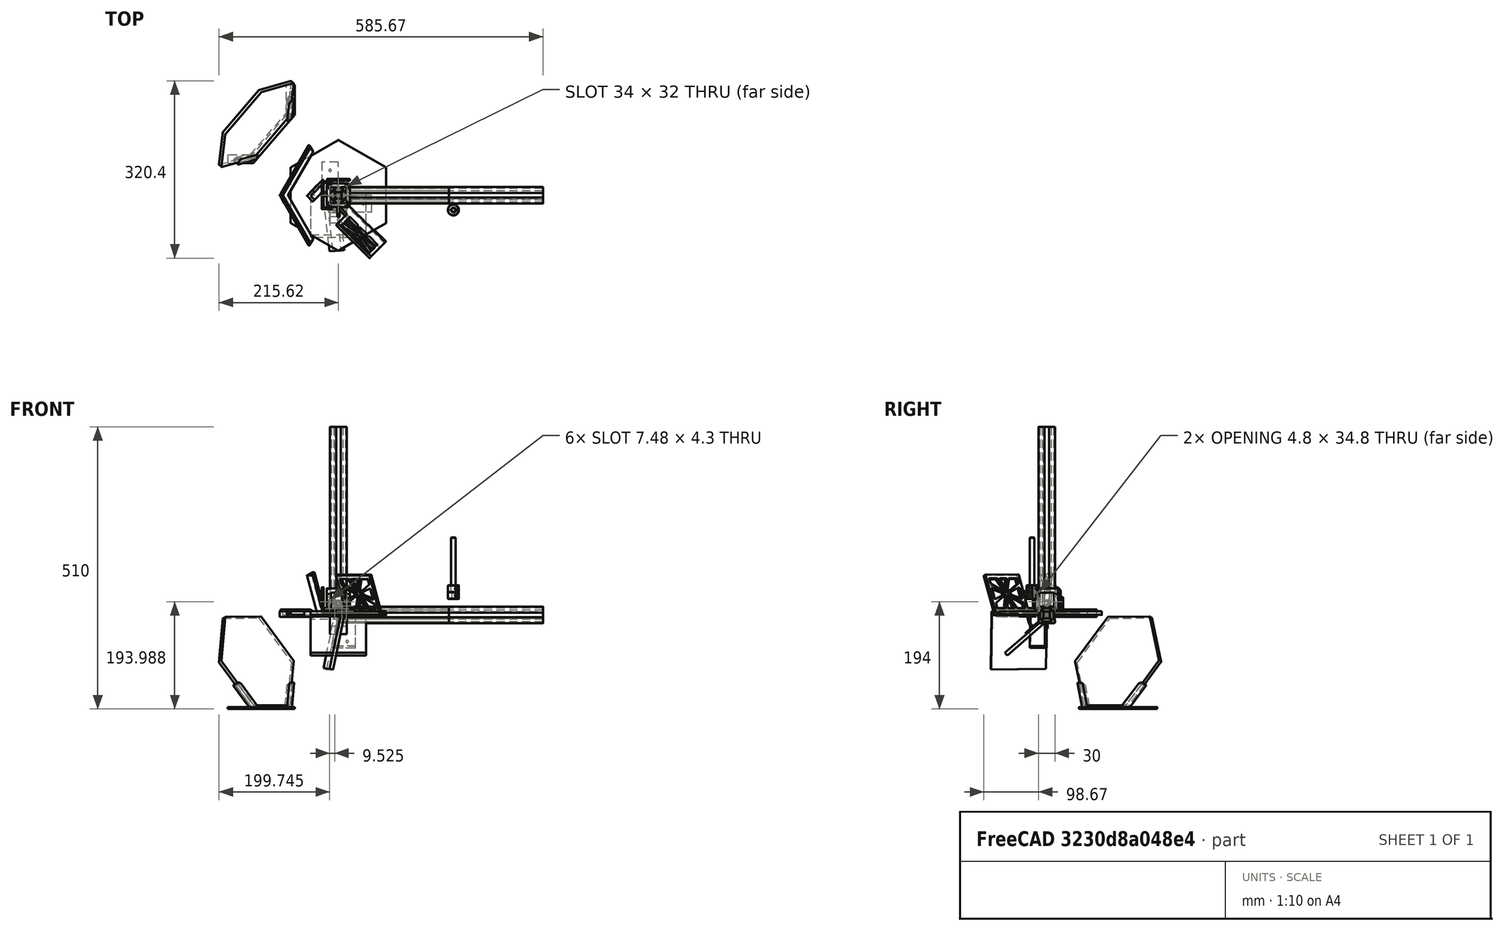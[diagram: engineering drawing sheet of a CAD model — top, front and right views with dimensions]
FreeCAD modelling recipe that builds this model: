
FCSTD DOCUMENT  (FreeCAD 1.1RUnknown)
Label: frame
License: All rights reserved
LicenseURL: https://en.wikipedia.org/wiki/All_rights_reserved
objects: App::Link×33, Sketcher::SketchObject×33, App::Point×32, App::Part×20, PartDesign::Pad×20, Part::Feature×15, PartDesign::Body×12, PartDesign::Fillet×12, PartDesign::Plane×11, PartDesign::Pocket×8, Part::Extrusion×3, Mesh::Feature×3, PartDesign::SubShapeBinder×3, PartDesign::AdditivePipe×2, PartDesign::Boolean×2, PartDesign::SubtractivePipe×2, Spreadsheet::Sheet×1, PartDesign::AdditiveBox×1, Part::Box×1, PartDesign::Mirrored×1, +2 more types
note: 252 computed .brp shape members not serialized (recipe doc carries the construction recipe); baked Part::Feature solids carry a one-line shape summary decoded from their .brp

FEATURE [PartDesign::Body] Body
  AllowCompound = false
  Origin = -> Origin
FEATURE [Spreadsheet::Sheet] Spreadsheet
  cells = A1='Extrusion length:; B1(EL)==200 mm; D1='Extrusion width; E1==30 mm; G1='Mirror thickness; H1==0.25 in; M1='Rail thickness; N1==3 mm; O1==H1 + H6 + N1 * 2; A2='Cube size:; B2==2.2 in; C2==-B2 / 2; D2='Extrusion radius; E2==E1 / 2; G2='Mount thickness; H2==3 mm; M2='Rail width; N2==8 mm; A3='Frame distance:; B3==B1 - B6 + E1; G3='Flange width; H3==8 mm; M3='Rail length; N3==50 mm; A4='Motor distance; B4==170 mm; C4==B4 - 150 mm; D4='Before (152.25mm); G4='Edge width; H4==5 mm; A5='Motor offset; B5==45 mm; G5='Edge height; H5==H1 + H2 + H6 * 2; A6='Inset amount; B6==45 mm; G6='Mirror tolerance; H6==0.5 mm; G7='Mirror width; H7==200 mm; A8='Length 2; B8==B1; A9='Length 3; B9==B3 * 2; G9='Cover height; H9==3 mm; J9='Total height; K9==H5 + H9; A10='Length 4; B10==2 * B3 - E1; G10='Stretch amt; H10==1 mm; G11='Tab thickness; H11==3 mm; A12='Gripper dist; B12==B4 - 9 mm; G12='Tab distance; H12==H7 / 2 + I12; I12==2.5 mm; A14='Robot Radius; B14==B1; G14='Tab width; H14==15 mm; G15='Extra space; H15==10 mm; M15='Square mirror width; N15==100 mm; G16='Tab space; H16==H14 + H15; M16='Mirror 1 angle; N16=41; G18='Pin dist; H18==30 mm; G19='Square dist; H19==H18 - H4 / 2; A20='Phone dims; G20='Pin diameter; H20==3 mm; A21='Height; B21==80 mm; G21='Pin tolerance; H21==0.5 mm; A22='Cameras; B22==70 mm; A23='Phone width; B23==10 mm; G23='Plate Snapper Gap; H23==0.5 mm; A24='Holder width; B24==160 mm
FEATURE [PartDesign::AdditiveBox] Box
  AttacherType = Attacher::AttachEngine3D
  AttachmentOffset = pos=(-27.94,-27.94,-27.94) rot=(0,0,1;0rad)
  AttachmentSupport = -> [XY_Plane002]
  Height = 55.88
  Length = 55.88
  MapMode = 5
  Placement = pos=(-27.94,-27.94,-27.94) rot=(0,0,1;0rad)
  Refine = true
  Suppressed = false
  Width = 55.88
  expr: .AttachmentOffset.Base.x = Spreadsheet.C2
  expr: .AttachmentOffset.Base.y = Spreadsheet.C2
  expr: .AttachmentOffset.Base.z = Spreadsheet.C2
  expr: Height = Spreadsheet.B2
  expr: Length = Spreadsheet.B2
  expr: Width = Spreadsheet.B2
FEATURE [App::Part] Part001  label="Rubik's Cube"
  Group = -> [Box]
  Origin = -> Origin002
FEATURE [Part::Box] Box001  label="Cube"
  AttacherType = Attacher::AttachEngine3D
  Height = 25
  Length = 200
  Placement = pos=(0,-12.5,-12.5) rot=(0,0,1;0rad)
  Width = 25
  expr: Length = Spreadsheet.B1
FEATURE [App::Link] Link001  label="Rubik's Cube001"
  LinkedObject = -> Part001
FEATURE [App::Link] Link004  label="Extrusion004"
  LinkPlacement = pos=(-45,-30,185) rot=(0,0,1;1.5708rad)
  LinkedObject = -> Part
  Placement = pos=(-45,-30,185) rot=(0,0,1;1.5708rad)
  expr: .Placement.Base.x = -Spreadsheet.B5
  expr: .Placement.Base.y = Spreadsheet.E2 - Spreadsheet.B6
  expr: .Placement.Base.z = Spreadsheet.B3
FEATURE [Part::Feature] Part__Feature001  label="bkt08a"
  Placement = pos=(-20.7,26.4,0) rot=(0.707107,0,0.707107;3.14159rad)
  shape: bbox 41.3 x 51 x 35 mm, 84 faces (baked)
FEATURE [App::Link] Link011  label="Motor mount001"
  LinkPlacement = pos=(0,0,170) rot=(0,0,1;1.5708rad)
  LinkedObject = -> Part003
  Placement = pos=(0,0,170) rot=(0,0,1;1.5708rad)
  expr: .Placement.Base.z = Spreadsheet.B4
FEATURE [App::Link] Link012  label="Motor mount002"
  LinkPlacement = pos=(0,170,0) rot=(1,0,0;-1.5708rad)
  LinkedObject = -> Part003
  Placement = pos=(0,170,0) rot=(1,0,0;-1.5708rad)
  expr: .Placement.Base.y = Spreadsheet.B4
FEATURE [App::Link] Link013  label="Motor mount003"
  LinkPlacement = pos=(0,0,-170) rot=(1,0,0;3.14159rad)
  LinkedObject = -> Part003
  Placement = pos=(0,0,-170) rot=(1,0,0;3.14159rad)
  expr: .Placement.Base.z = -Spreadsheet.B4
FEATURE [App::Link] Link014  label="Motor mount004"
  LinkPlacement = pos=(0,-170,0) rot=(1,0,0;1.5708rad)
  LinkedObject = -> Part003
  Placement = pos=(0,-170,0) rot=(1,0,0;1.5708rad)
  expr: .Placement.Base.y = -Spreadsheet.B4
FEATURE [App::Link] Link015  label="Motor mount005"
  LinkPlacement = pos=(170,0,0) rot=(1,-1,1;4.18879rad)
  LinkedObject = -> Part003
  Placement = pos=(170,0,0) rot=(1,-1,1;4.18879rad)
  expr: .Placement.Base.x = Spreadsheet.B4
FEATURE [App::Link] Link016  label="Motor mount006"
  LinkPlacement = pos=(-170,0,0) rot=(1,1,-1;4.18879rad)
  LinkedObject = -> Part003
  Placement = pos=(-170,0,0) rot=(1,1,-1;4.18879rad)
  expr: .Placement.Base.x = -Spreadsheet.B4
FEATURE [Part::Feature] Part__Feature  label="17HS19-2004S1"
  shape: bbox 42.32 x 71.15 x 72 mm, 281 faces (baked)
FEATURE [Sketcher::SketchObject] Sketch001
  ArcFitTolerance = 1e-06
  AttachmentSupport = -> [YZ_Plane]
  ExternalTypes = [0]
  FullyConstrained = true
  MakeInternals = false
  MapMode = 5
  Placement = pos=(0,0,0) rot=(0.57735,0.57735,0.57735;2.0944rad)
  _ExternalGeoVersion = 0
  sketch-geometry (67):
    g0: LineSegment StartX=-3.2886 StartY=5.82 StartZ=0 EndX=3.2886 EndY=5.82 EndZ=0
    g1: LineSegment StartX=-3.2886 StartY=-5.82 StartZ=0 EndX=3.2886 EndY=-5.82 EndZ=0
    g2: LineSegment StartX=5.82 StartY=-3.2886 StartZ=0 EndX=5.82 EndY=3.2886 EndZ=0
    g3: LineSegment StartX=-5.82 StartY=-3.2886 StartZ=0 EndX=-5.82 EndY=3.2886 EndZ=0
    g4: LineSegment [constr] StartX=-15.0006 StartY=-15.0006 StartZ=0 EndX=14.9994 EndY=14.9994 EndZ=0
    g5: ArcOfCircle CenterX=7.59529 CenterY=3.2886 CenterZ=0 NormalX=0 NormalY=0 NormalZ=1 AngleXU=0 Radius=1.77529 StartAngle=2.35619 EndAngle=3.14159
    g6: ArcOfCircle CenterX=3.2886 CenterY=7.59529 CenterZ=0 NormalX=0 NormalY=0 NormalZ=1 AngleXU=0 Radius=1.77529 StartAngle=4.71239 EndAngle=5.49779
    g7: ArcOfCircle CenterX=-3.2886 CenterY=7.59529 CenterZ=0 NormalX=0 NormalY=0 NormalZ=1 AngleXU=0 Radius=1.77529 StartAngle=3.92699 EndAngle=4.71239
    g8: ArcOfCircle CenterX=-7.59529 CenterY=3.2886 CenterZ=0 NormalX=0 NormalY=0 NormalZ=1 AngleXU=0 Radius=1.77529 StartAngle=5e-16 EndAngle=0.785398
    g9: ArcOfCircle CenterX=-7.59529 CenterY=-3.2886 CenterZ=0 NormalX=0 NormalY=0 NormalZ=1 AngleXU=0 Radius=1.77529 StartAngle=5.49779 EndAngle=6.28319
    g10: ArcOfCircle CenterX=-3.2886 CenterY=-7.59529 CenterZ=0 NormalX=0 NormalY=0 NormalZ=1 AngleXU=0 Radius=1.77529 StartAngle=1.5708 EndAngle=2.35619
    g11: ArcOfCircle CenterX=3.2886 CenterY=-7.59529 CenterZ=0 NormalX=0 NormalY=0 NormalZ=1 AngleXU=0 Radius=1.77529 StartAngle=0.785398 EndAngle=1.5708
    g12: ArcOfCircle CenterX=7.59529 CenterY=-3.2886 CenterZ=0 NormalX=0 NormalY=0 NormalZ=1 AngleXU=0 Radius=1.77529 StartAngle=3.14159 EndAngle=3.92699
    g13: LineSegment [constr] StartX=-14.9994 StartY=14.9994 StartZ=0 EndX=15.0006 EndY=-15.0006 EndZ=0
    g14: LineSegment StartX=4.54392 StartY=6.33997 StartZ=0 EndX=7.73503 EndY=9.53108 EndZ=0
    g15: LineSegment StartX=6.33997 StartY=4.54392 StartZ=0 EndX=9.53108 EndY=7.73503 EndZ=0
    g16: LineSegment StartX=6.33997 StartY=-4.54392 StartZ=0 EndX=9.53108 EndY=-7.73503 EndZ=0
    g17: LineSegment StartX=4.54392 StartY=-6.33997 StartZ=0 EndX=7.73503 EndY=-9.53108 EndZ=0
    g18: LineSegment StartX=-4.54392 StartY=-6.33997 StartZ=0 EndX=-7.73503 EndY=-9.53108 EndZ=0
    g19: LineSegment StartX=-6.33997 StartY=-4.54392 StartZ=0 EndX=-9.53108 EndY=-7.73503 EndZ=0
    g20: LineSegment StartX=-4.54392 StartY=6.33997 StartZ=0 EndX=-7.73503 EndY=9.53108 EndZ=0
    g21: LineSegment StartX=-6.33997 StartY=4.54392 StartZ=0 EndX=-9.53108 EndY=7.73503 EndZ=0
    g22: ArcOfCircle CenterX=10.7864 CenterY=6.47971 CenterZ=0 NormalX=0 NormalY=0 NormalZ=1 AngleXU=0 Radius=1.77529 StartAngle=6.24828 EndAngle=8.63938
    g23: LineSegment StartX=12.5606 StartY=6.41776 StartZ=0 EndX=12.5184 EndY=5.20856 EndZ=0
    g24: LineSegment StartX=14.727 StartY=5.13144 StartZ=0 EndX=14.9994 EndY=12.9308 EndZ=0
    g25: ArcOfCircle CenterX=13.6227 CenterY=5.17 CenterZ=0 NormalX=0 NormalY=0 NormalZ=1 AngleXU=0 Radius=1.105 StartAngle=3.10669 EndAngle=6.24828
    g26: ArcOfCircle CenterX=6.47971 CenterY=10.7864 CenterZ=0 NormalX=0 NormalY=0 NormalZ=1 AngleXU=0 Radius=1.77529 StartAngle=5.49779 EndAngle=7.88889
    g27: ArcOfCircle CenterX=5.17 CenterY=13.6227 CenterZ=0 NormalX=0 NormalY=0 NormalZ=1 AngleXU=0 Radius=1.105 StartAngle=1.6057 EndAngle=4.7473
    g28: LineSegment StartX=5.20856 StartY=12.5184 StartZ=0 EndX=6.41776 EndY=12.5606 EndZ=0
    g29: LineSegment StartX=5.13144 StartY=14.727 StartZ=0 EndX=12.9308 EndY=14.9994 EndZ=0
    g30: ArcOfCircle CenterX=13.0006 CenterY=13.0006 CenterZ=0 NormalX=0 NormalY=0 NormalZ=1 AngleXU=0 Radius=2 StartAngle=6.24828 EndAngle=7.88889
    g31: LineSegment [constr] StartX=12.9308 StartY=14.9994 StartZ=0 EndX=14.9994 EndY=14.9994 EndZ=0
    g32: ArcOfCircle CenterX=-6.47971 CenterY=10.7864 CenterZ=0 NormalX=0 NormalY=0 NormalZ=1 AngleXU=0 Radius=1.77529 StartAngle=1.53589 EndAngle=3.92699
    g33: LineSegment StartX=-6.41776 StartY=12.5606 StartZ=0 EndX=-5.20856 EndY=12.5184 EndZ=0
    g34: LineSegment StartX=-5.13144 StartY=14.727 StartZ=0 EndX=-12.9308 EndY=14.9994 EndZ=0
    g35: ArcOfCircle CenterX=-5.17 CenterY=13.6227 CenterZ=0 NormalX=0 NormalY=0 NormalZ=1 AngleXU=0 Radius=1.105 StartAngle=4.67748 EndAngle=7.81907
    g36: ArcOfCircle CenterX=-10.7864 CenterY=6.47971 CenterZ=0 NormalX=0 NormalY=0 NormalZ=1 AngleXU=0 Radius=1.77529 StartAngle=0.785398 EndAngle=3.1765
    g37: ArcOfCircle CenterX=-13.6227 CenterY=5.17 CenterZ=0 NormalX=0 NormalY=0 NormalZ=1 AngleXU=0 Radius=1.105 StartAngle=3.1765 EndAngle=6.31809
    g38: LineSegment StartX=-12.5184 StartY=5.20856 StartZ=0 EndX=-12.5606 EndY=6.41776 EndZ=0
    g39: LineSegment StartX=-14.727 StartY=5.13144 StartZ=0 EndX=-14.9994 EndY=12.9308 EndZ=0
    g40: ArcOfCircle CenterX=-13.0006 CenterY=13.0006 CenterZ=0 NormalX=0 NormalY=0 NormalZ=1 AngleXU=0 Radius=2 StartAngle=1.53589 EndAngle=3.1765
    g41: ArcOfCircle CenterX=-10.7864 CenterY=-6.47971 CenterZ=0 NormalX=0 NormalY=0 NormalZ=1 AngleXU=0 Radius=1.77529 StartAngle=3.10669 EndAngle=5.49779
    g42: LineSegment StartX=-12.5606 StartY=-6.41776 StartZ=0 EndX=-12.5184 EndY=-5.20856 EndZ=0
    g43: LineSegment StartX=-14.727 StartY=-5.13144 StartZ=0 EndX=-14.9994 EndY=-12.9308 EndZ=0
    g44: ArcOfCircle CenterX=-13.6227 CenterY=-5.17 CenterZ=0 NormalX=0 NormalY=0 NormalZ=1 AngleXU=0 Radius=1.105 StartAngle=6.24828 EndAngle=9.38987
    g45: ArcOfCircle CenterX=-6.47971 CenterY=-10.7864 CenterZ=0 NormalX=0 NormalY=0 NormalZ=1 AngleXU=0 Radius=1.77529 StartAngle=2.35619 EndAngle=4.7473
    g46: ArcOfCircle CenterX=-5.17 CenterY=-13.6227 CenterZ=0 NormalX=0 NormalY=0 NormalZ=1 AngleXU=0 Radius=1.105 StartAngle=4.7473 EndAngle=7.88889
    g47: LineSegment StartX=-5.20856 StartY=-12.5184 StartZ=0 EndX=-6.41776 EndY=-12.5606 EndZ=0
    g48: LineSegment StartX=-5.13144 StartY=-14.727 StartZ=0 EndX=-12.9308 EndY=-14.9994 EndZ=0
    g49: ArcOfCircle CenterX=-13.0006 CenterY=-13.0006 CenterZ=0 NormalX=0 NormalY=0 NormalZ=1 AngleXU=0 Radius=2 StartAngle=3.10669 EndAngle=4.7473
    g50: ArcOfCircle CenterX=6.47971 CenterY=-10.7864 CenterZ=0 NormalX=0 NormalY=0 NormalZ=1 AngleXU=0 Radius=1.77529 StartAngle=4.67748 EndAngle=7.06858
    g51: LineSegment StartX=6.41776 StartY=-12.5606 StartZ=0 EndX=5.20856 EndY=-12.5184 EndZ=0
    g52: LineSegment StartX=5.13144 StartY=-14.727 StartZ=0 EndX=12.9308 EndY=-14.9994 EndZ=0
    g53: ArcOfCircle CenterX=5.17 CenterY=-13.6227 CenterZ=0 NormalX=0 NormalY=0 NormalZ=1 AngleXU=0 Radius=1.105 StartAngle=1.53589 EndAngle=4.67748
    g54: ArcOfCircle CenterX=10.7864 CenterY=-6.47971 CenterZ=0 NormalX=0 NormalY=0 NormalZ=1 AngleXU=0 Radius=1.77529 StartAngle=3.92699 EndAngle=6.31809
    g55: ArcOfCircle CenterX=13.6227 CenterY=-5.17 CenterZ=0 NormalX=0 NormalY=0 NormalZ=1 AngleXU=0 Radius=1.105 StartAngle=0.0349067 EndAngle=3.1765
    g56: LineSegment StartX=12.5184 StartY=-5.20856 StartZ=0 EndX=12.5606 EndY=-6.41776 EndZ=0
    g57: LineSegment StartX=14.727 StartY=-5.13144 StartZ=0 EndX=14.9994 EndY=-12.9308 EndZ=0
    g58: ArcOfCircle CenterX=13.0006 CenterY=-13.0006 CenterZ=0 NormalX=0 NormalY=0 NormalZ=1 AngleXU=0 Radius=2 StartAngle=4.67748 EndAngle=6.31809
    g59: LineSegment [constr] StartX=13.6227 StartY=4.065 StartZ=0 EndX=13.6227 EndY=-4.065 EndZ=0
    g60: LineSegment [constr] StartX=10.7864 StartY=8.255 StartZ=0 EndX=10.7864 EndY=-8.255 EndZ=0
    g61: LineSegment [constr] StartX=-6.47971 StartY=-12.5617 StartZ=0 EndX=0 EndY=-12.5617 EndZ=0
    g62: LineSegment [constr] StartX=-15.0006 StartY=-15.0006 StartZ=0 EndX=-13.0006 EndY=-15.0006 EndZ=0
    g63: LineSegment [constr] StartX=-6.41776 StartY=12.5606 StartZ=0 EndX=-6.34063 EndY=14.7693 EndZ=0
    g64: LineSegment [constr] StartX=12.5184 StartY=5.20856 StartZ=0 EndX=14.727 EndY=5.13144 EndZ=0
    g65: LineSegment [constr] StartX=-14.727 StartY=-5.13144 StartZ=0 EndX=-12.5184 EndY=-5.20856 EndZ=0
    g66: LineSegment [constr] StartX=5.20856 StartY=-12.5184 StartZ=0 EndX=5.13144 EndY=-14.727 EndZ=0
  constraints (151):
    c: Horizontal(g0)
    c: Vertical(g2)
    c: Distance(g1,g0) = 11.64
    c: Symmetric(g0,g1,g-1)
    c: Symmetric(g2,g3,g-2)
    c: Symmetric(g0,g2,g4)
    c: DistanceY(g4,g4) = 30
    c: Tangent(g5,g2) = 1.5708
    c: Equal(g10,g11)
    c: Tangent(g6,g0) = -1.5708
    c: Tangent(g7,g0) = -1.5708
    c: Tangent(g8,g3) = -1.5708
    c: Tangent(g9,g3) = -1.5708
    c: Tangent(g10,g1) = 1.5708
    c: Tangent(g11,g1) = 1.5708
    c: Tangent(g12,g2) = 1.5708
    c: Symmetric(g5,g6,g4)
    c: Symmetric(g7,g12,g4)
    c: Symmetric(g8,g11,g4)
    c: Symmetric(g9,g10,g4)
    c: Equal(g13,g4)
    c: Symmetric(g13,g4,g-2)
    c: Symmetric(g7,g6,g-2)
    c: Symmetric(g7,g8,g13)
    c: Tangent(g14,g6) = -1.5708
    c: Tangent(g15,g5) = 1.5708
    c: Tangent(g18,g10) = -1.5708
    c: Tangent(g19,g9) = 1.5708
    c: Tangent(g20,g7) = 1.5708
    c: Tangent(g21,g8) = -1.5708
    c: Tangent(g17,g11) = 1.5708
    c: Symmetric(g14,g15,g4)
    c: Distance(g15,g14) = 2.54
    c: Tangent(g16,g12) = -1.5708
    c: Symmetric(g19,g18,g4)
    c: Parallel(g19,g4)
    c: Symmetric(g16,g17,g13)
    c: Symmetric(g20,g21,g13)
    c: Parallel(g20,g13)
    c: Equal(g17,g18)
    c: Equal(g19,g21)
    c: Equal(g20,g14)
    c: Tangent(g25,g23) = -1.5708
    c: Tangent(g25,g24) = -1.5708
    c: Tangent(g23,g22) = 1.5708
    c: Tangent(g22,g15) = 1.5708
    c: Tangent(g30,g24) = -1.5708
    c: Tangent(g30,g29) = 1.5708
    c: Tangent(g28,g26) = 1.5708
    c: Tangent(g26,g14) = -1.5708
    c: Tangent(g28,g27) = -1.5708
    c: Tangent(g29,g27) = 1.5708
    c: Parallel(g29,g28)
    c: Parallel(g23,g24)
    c: Symmetric(g27,g24,g4)
    c: Distance(g24,g23) = 2.21
    c: Angle(g29,g24) = 1.50098
    c: Coincident(g31,g29)
    c: Coincident(g31,g4)
    c: Horizontal(g31)
    c: Tangent(g35,g33) = -1.5708
    c: Tangent(g44,g42) = -1.5708
    c: Tangent(g53,g51) = -1.5708
    c: Tangent(g35,g34) = -1.5708
    c: Tangent(g44,g43) = -1.5708
    c: Tangent(g53,g52) = -1.5708
    c: Tangent(g33,g32) = 1.5708
    c: Tangent(g42,g41) = 1.5708
    c: Tangent(g51,g50) = 1.5708
    c: Tangent(g40,g34) = -1.5708
    c: Tangent(g49,g43) = -1.5708
    c: Tangent(g58,g52) = -1.5708
    c: Tangent(g40,g39) = 1.5708
    c: Tangent(g49,g48) = 1.5708
    c: Tangent(g58,g57) = 1.5708
    c: Tangent(g38,g36) = 1.5708
    c: Tangent(g47,g45) = 1.5708
    c: Tangent(g56,g54) = 1.5708
    c: Tangent(g38,g37) = -1.5708
    c: Tangent(g47,g46) = -1.5708
    c: Tangent(g56,g55) = -1.5708
    c: Tangent(g39,g37) = 1.5708
    c: Tangent(g48,g46) = 1.5708
    c: Tangent(g57,g55) = 1.5708
    c: Parallel(g39,g38)
    c: Parallel(g48,g47)
    c: Parallel(g57,g56)
    c: Parallel(g33,g34)
    c: Parallel(g42,g43)
    c: Parallel(g51,g52)
    c: Equal(g37,g35)
    c: Equal(g46,g44)
    c: Equal(g55,g53)
    c: Angle(g39,g34) = 1.50098
    c: Angle(g48,g43) = 1.50098
    c: Angle(g57,g52) = 1.50098
    c: Symmetric(g35,g37,g13)
    c: Tangent(g21,g36) = -1.5708
    c: Tangent(g32,g20) = 1.5708
    c: Tangent(g45,g18) = -1.5708
    c: Tangent(g41,g19) = 1.5708
    c: Tangent(g50,g17) = 1.5708
    c: Tangent(g54,g16) = -1.5708
    c: Symmetric(g44,g46,g4)
    c: Symmetric(g55,g53,g13)
    c: PointOnObject(g59,g25)
    c: PointOnObject(g59,g55)
    c: Vertical(g59)
    c: Perpendicular(g25,g59)
    c: DistanceY(g59,g59) = 8.13
    c: Equal(g5,g22)
    c: PointOnObject(g60,g22)
    c: PointOnObject(g60,g54)
    c: Vertical(g60)
    c: Perpendicular(g22,g60)
    c: Perpendicular(g54,g60)
    c: DistanceY(g60,g60) = 16.51
    c: Symmetric(g27,g25,g4)
    c: Symmetric(g27,g35,g-2)
    c: Symmetric(g37,g44,g-1)
    c: Symmetric(g46,g53,g-2)
    c: Horizontal(g61)
    c: Tangent(g61,g45) = -1.5708
    c: Distance(g1,g61) = 6.74168
    c: Equal(g30,g40)
    c: Radius(g30) = 2
    c: PointOnObject(g40,g13)
    c: Equal(g40,g49)
    c: Equal(g58,g49)
    c: PointOnObject(g61,g-2)
    c: PointOnObject(g-1,g13)
    c: PointOnObject(g-1,g4)
    c: Coincident(g62,g4)
    c: Horizontal(g62)
    c: Tangent(g62,g49) = -1.5708
    c: PointOnObject(g58,g13)
    c: PointOnObject(g49,g4)
    c: Parallel(g14,g15)
    c: PointOnObject(g63,g34)
    c: Perpendicular(g33,g63)
    c: Coincident(g63,g32)
    c: Coincident(g64,g23)
    c: Coincident(g64,g24)
    c: Equal(g63,g64)
    c: Coincident(g65,g43)
    c: Coincident(g65,g42)
    c: Equal(g65,g64)
    c: Coincident(g66,g51)
    c: Coincident(g66,g52)
    c: Equal(g64,g66)
    c: Horizontal(g1)
FEATURE [PartDesign::Pad] Pad
  Direction = (1,0,0)
  Length = 200
  Length2 = 10
  Placement = pos=(0,0,0) rot=(1,1,1;2.0944rad)
  Profile = -> Sketch001
  ReferenceAxis = -> Sketch001 [N_Axis]
  Refine = true
  SideType = 0
  Suppressed = false
  Type = 0
  Type2 = 0
  expr: Length = Spreadsheet.B1
FEATURE [App::Part] Part  label="Extrusion"
  Group = -> [Box001,Sketch001,Pad]
  Origin = -> Origin001
FEATURE [Part::Feature] Part__Feature002  label="ST-M1"
  Placement = pos=(0,0,-3) rot=(0,0,1;4.71239rad)
  shape: bbox 52.7 x 50 x 53 mm, 170 faces (baked)
  expr: .Placement.Base.z = -3 mm
FEATURE [App::Part] Part003  label="Motor mount"
  Group = -> [Part__Feature001,Part__Feature,Part__Feature002]
  Origin = -> Origin004
FEATURE [App::Link] Link018  label="Sketch003"
  LinkedObject = -> Sketch001
FEATURE [Part::Extrusion] Extrude001
  Base = -> Link018
  Dir = (0,0,1)
  DirMode = 2
  FaceMakerClass = Part::FaceMakerBullseye
  FaceMakerMode = 3
  InnerWireTaper = 1
  LengthFwd = 370
  LengthRev = 0
  Placement = pos=(0,0,0) rot=(0,1,0;1.5708rad)
  Solid = true
  Symmetric = false
  expr: LengthFwd = Spreadsheet.B9
FEATURE [App::Part] Part005  label="Extrusion 3"
  Group = -> [Link018,Extrude001]
  Origin = -> Origin006
FEATURE [App::Link] Link019  label="Extrusion 004"
  LinkPlacement = pos=(-45,185,-170) rot=(0,1,0;-1.5708rad)
  LinkedObject = -> Part005
  Placement = pos=(-45,185,-170) rot=(0,1,0;-1.5708rad)
  expr: .Placement.Base.x = -Spreadsheet.B5
  expr: .Placement.Base.y = Spreadsheet.B3
  expr: .Placement.Base.z = -Spreadsheet.B3 + Spreadsheet.E2
FEATURE [App::Link] Link020  label="Extrusion 005"
  LinkPlacement = pos=(185,45,-170) rot=(0,1,0;-1.5708rad)
  LinkedObject = -> Part005
  Placement = pos=(185,45,-170) rot=(0,1,0;-1.5708rad)
  expr: .Placement.Base.x = Spreadsheet.B3
  expr: .Placement.Base.y = Spreadsheet.B5
  expr: .Placement.Base.z = -Spreadsheet.B3 + Spreadsheet.E2
FEATURE [App::Link] Link021  label="Extrusion 006"
  LinkPlacement = pos=(-185,-45,-170) rot=(0,1,0;-1.5708rad)
  LinkedObject = -> Part005
  Placement = pos=(-185,-45,-170) rot=(0,1,0;-1.5708rad)
  expr: .Placement.Base.x = -Spreadsheet.B3
  expr: .Placement.Base.y = -Spreadsheet.B5
  expr: .Placement.Base.z = -Spreadsheet.B3 + Spreadsheet.E2
FEATURE [App::Link] Link022  label="Extrusion009"
  LinkPlacement = pos=(-30,45,185) rot=(0,0,1;0rad)
  LinkedObject = -> Part
  Placement = pos=(-30,45,185) rot=(0,0,1;0rad)
  expr: .Placement.Base.x = -Spreadsheet.B6 + Spreadsheet.E2
  expr: .Placement.Base.y = Spreadsheet.B5
  expr: .Placement.Base.z = Spreadsheet.B3
FEATURE [App::Link] Link024  label="Sketch004"
  LinkedObject = -> Sketch001
FEATURE [Part::Extrusion] Extrude
  Base = -> Link024
  Dir = (0,0,1)
  DirMode = 2
  FaceMakerClass = Part::FaceMakerBullseye
  FaceMakerMode = 3
  InnerWireTaper = 1
  LengthFwd = 200
  LengthRev = 0
  Placement = pos=(0,0,0) rot=(0,1,0;1.5708rad)
  Solid = true
  Symmetric = false
  expr: LengthFwd = Spreadsheet.B8
FEATURE [App::Part] Part006  label="Extrusion 2"
  Group = -> [Link024,Extrude]
  Origin = -> Origin007
FEATURE [App::Link] Link025  label="Extrusion 007"
  LinkPlacement = pos=(-45,-185,-170) rot=(0,1,0;-1.5708rad)
  LinkedObject = -> Part006
  Placement = pos=(-45,-185,-170) rot=(0,1,0;-1.5708rad)
  expr: .Placement.Base.x = -Spreadsheet.B5
  expr: .Placement.Base.y = -Spreadsheet.B3
  expr: .Placement.Base.z = -Spreadsheet.B3 + Spreadsheet.E2
FEATURE [App::Link] Link026  label="Extrusion 008"
  LinkPlacement = pos=(-170,-45,185) rot=(0,0,1;0rad)
  LinkedObject = -> Part006
  Placement = pos=(-170,-45,185) rot=(0,0,1;0rad)
  expr: .Placement.Base.x = -Spreadsheet.E2 + Spreadsheet.B6 - Spreadsheet.B1
  expr: .Placement.Base.y = -Spreadsheet.B5
  expr: .Placement.Base.z = Spreadsheet.B3
FEATURE [App::Link] Link031  label="Sketch005"
  LinkedObject = -> Sketch001
FEATURE [Part::Extrusion] Extrude002
  Base = -> Link031
  Dir = (0,0,1)
  DirMode = 2
  FaceMakerClass = Part::FaceMakerBullseye
  FaceMakerMode = 3
  InnerWireTaper = 1
  LengthFwd = 340
  LengthRev = 0
  Solid = true
  Symmetric = false
  expr: LengthFwd = Spreadsheet.B10
FEATURE [App::Part] Part007  label="Extrusion 4"
  Group = -> [Link031,Extrude002]
  Origin = -> Origin008
FEATURE [App::Link] Link  label="Extrusion 009"
  LinkPlacement = pos=(-200,185,-185) rot=(0,0,1;0rad)
  LinkedObject = -> Part005
  Placement = pos=(-200,185,-185) rot=(0,0,1;0rad)
  expr: .Placement.Base.x = -Spreadsheet.B3 - Spreadsheet.E2
  expr: .Placement.Base.y = Spreadsheet.B3
  expr: .Placement.Base.z = -Spreadsheet.B3
FEATURE [App::Link] Link032  label="Extrusion 010"
  LinkPlacement = pos=(-185,-200,-185) rot=(0,0,1;1.5708rad)
  LinkedObject = -> Part005
  Placement = pos=(-185,-200,-185) rot=(0,0,1;1.5708rad)
  expr: .Placement.Base.x = -Spreadsheet.B3
  expr: .Placement.Base.y = -Spreadsheet.B3 - Spreadsheet.E2
  expr: .Placement.Base.z = -Spreadsheet.B3
FEATURE [App::Link] Link033  label="Extrusion 011"
  LinkPlacement = pos=(200,-185,-185) rot=(0,0,1;3.14159rad)
  LinkedObject = -> Part005
  Placement = pos=(200,-185,-185) rot=(0,0,1;3.14159rad)
  expr: .Placement.Base.x = Spreadsheet.B3 + Spreadsheet.E2
  expr: .Placement.Base.y = -Spreadsheet.B3
  expr: .Placement.Base.z = -Spreadsheet.B3
FEATURE [App::Link] Link034  label="Extrusion 012"
  LinkPlacement = pos=(185,200,-185) rot=(0,0,1;-1.5708rad)
  LinkedObject = -> Part005
  Placement = pos=(185,200,-185) rot=(0,0,1;-1.5708rad)
  expr: .Placement.Base.x = Spreadsheet.B3
  expr: .Placement.Base.y = Spreadsheet.B3 + Spreadsheet.E2
  expr: .Placement.Base.z = -Spreadsheet.B3
FEATURE [App::Link] Link035  label="Extrusion 013"
  LinkPlacement = pos=(-45,170,-185) rot=(1,0,0;1.5708rad)
  LinkedObject = -> Part007
  Placement = pos=(-45,170,-185) rot=(1,0,0;1.5708rad)
  expr: .Placement.Base.x = -Spreadsheet.B6
  expr: .Placement.Base.y = Spreadsheet.B3 - Spreadsheet.E2
  expr: .Placement.Base.z = -Spreadsheet.B3
FEATURE [App::Link] Link036  label="Gripper001"
  LinkedObject = -> Part008
FEATURE [App::Link] Link037  label="Gripper002"
  LinkPlacement = pos=(0,0,0) rot=(0,1,0;1.5708rad)
  LinkedObject = -> Part008
  Placement = pos=(0,0,0) rot=(0,1,0;1.5708rad)
FEATURE [App::Link] Link038  label="Gripper003"
  LinkPlacement = pos=(0,0,0) rot=(0,1,0;-1.5708rad)
  LinkedObject = -> Part008
  Placement = pos=(0,0,0) rot=(0,1,0;-1.5708rad)
FEATURE [App::Link] Link039  label="Gripper004"
  LinkPlacement = pos=(0,0,0) rot=(1,0,0;1.5708rad)
  LinkedObject = -> Part008
  Placement = pos=(0,0,0) rot=(1,0,0;1.5708rad)
FEATURE [App::Link] Link040  label="Gripper005"
  LinkPlacement = pos=(0,0,0) rot=(1,0,0;-1.5708rad)
  LinkedObject = -> Part008
  Placement = pos=(0,0,0) rot=(1,0,0;-1.5708rad)
FEATURE [App::Link] Link041  label="Gripper006"
  LinkPlacement = pos=(0,0,0) rot=(0,1,0;3.14159rad)
  LinkedObject = -> Part008
  Placement = pos=(0,0,0) rot=(0,1,0;3.14159rad)
FEATURE [Mesh::Feature] cube_gripper_2  label="cube_gripper.2"
  Placement = pos=(0,0,-161) rot=(0,1,0;3.14159rad)
  expr: .Placement.Base.z = -Spreadsheet.B12
FEATURE [Mesh::Feature] cube_gripper_stl
  Placement = pos=(0,0,-161) rot=(0,1,0;3.14159rad)
  expr: .Placement.Base.z = -Spreadsheet.B12
FEATURE [Mesh::Feature] cube_gripper_3  label="cube_gripper.3"
  Placement = pos=(0,0,-161) rot=(0,1,0;3.14159rad)
  expr: .Placement.Base.z = -Spreadsheet.B12
FEATURE [Sketcher::SketchObject] Sketch
  ArcFitTolerance = 1e-06
  AttachmentSupport = -> [XY_Plane011]
  ExternalTypes = [0]
  FullyConstrained = true
  MakeInternals = false
  MapMode = 5
  _ExternalGeoVersion = 0
  expr: Constraints[19] = Spreadsheet.H7
  sketch-geometry (7):
    g0: LineSegment StartX=-50 StartY=86.6025 StartZ=0 EndX=-100 EndY=0 EndZ=0
    g1: LineSegment StartX=-100 StartY=0 StartZ=0 EndX=-50 EndY=-86.6025 EndZ=0
    g2: LineSegment StartX=-50 StartY=-86.6025 StartZ=0 EndX=50 EndY=-86.6025 EndZ=0
    g3: LineSegment StartX=50 StartY=-86.6025 StartZ=0 EndX=100 EndY=-1.42e-14 EndZ=0
    g4: LineSegment StartX=100 StartY=-1.42e-14 StartZ=0 EndX=50 EndY=86.6025 EndZ=0
    g5: LineSegment StartX=50 StartY=86.6025 StartZ=0 EndX=-50 EndY=86.6025 EndZ=0
    g6: Circle [constr] CenterX=0 CenterY=0 CenterZ=0 NormalX=0 NormalY=0 NormalZ=1 AngleXU=0 Radius=100
  constraints (16):
    c: Coincident(g0,g1)
    c: Coincident(g1,g2)
    c: Coincident(g2,g3)
    c: Coincident(g3,g4)
    c: Coincident(g4,g5)
    c: Coincident(g5,g0)
    c: Equal(g0, g1-g5) x5
    c: PointOnObject(g0,g6)
    c: PointOnObject(g1,g6)
    c: PointOnObject(g2,g6)
    c: PointOnObject(g3,g6)
    c: PointOnObject(g4,g6)
    c: PointOnObject(g5,g6)
    c: Coincident(g6,g-1)
    c: Horizontal(g5)
    c: Diameter(g6) = 200
FEATURE [PartDesign::Pad] Pad001
  Direction = (0,0,1)
  Length = 6.35
  Length2 = 10
  Profile = -> Sketch
  ReferenceAxis = -> Sketch [N_Axis]
  Refine = true
  SideType = 0
  Suppressed = false
  Type = 0
  Type2 = 0
  expr: Length = Spreadsheet.H1
FEATURE [Sketcher::SketchObject] Sketch002
  ArcFitTolerance = 1e-06
  AttachmentSupport = -> [XY_Plane013]
  ExternalTypes = [0]
  FullyConstrained = true
  MakeInternals = false
  MapMode = 5
  _ExternalGeoVersion = 0
  expr: Constraints[19] = Spreadsheet.H7 + Spreadsheet.H6
  expr: Constraints[34] = Spreadsheet.H3
  sketch-geometry (13):
    g0: LineSegment [constr] StartX=50.125 StartY=-86.819 StartZ=0 EndX=100.25 EndY=-5.684e-13 EndZ=0
    g1: LineSegment [constr] StartX=100.25 StartY=-5.684e-13 StartZ=0 EndX=50.125 EndY=86.819 EndZ=0
    g2: LineSegment [constr] StartX=50.125 StartY=86.819 StartZ=0 EndX=-50.125 EndY=86.819 EndZ=0
    g3: LineSegment StartX=-50.125 StartY=86.819 StartZ=0 EndX=-100.25 EndY=1.99e-13 EndZ=0
    g4: LineSegment StartX=-100.25 StartY=1.99e-13 StartZ=0 EndX=-50.125 EndY=-86.819 EndZ=0
    g5: LineSegment [constr] StartX=-50.125 StartY=-86.819 StartZ=0 EndX=50.125 EndY=-86.819 EndZ=0
    g6: Circle [constr] CenterX=0 CenterY=0 CenterZ=0 NormalX=0 NormalY=0 NormalZ=1 AngleXU=0 Radius=100.25
    g7: LineSegment [constr] StartX=0 StartY=0 StartZ=0 EndX=-50.125 EndY=86.819 EndZ=0
    g8: LineSegment [constr] StartX=0 StartY=0 StartZ=0 EndX=-50.125 EndY=-86.819 EndZ=0
    g9: LineSegment StartX=-50.125 StartY=-86.819 StartZ=0 EndX=-45.5062 EndY=-78.819 EndZ=0
    g10: LineSegment StartX=-50.125 StartY=86.819 StartZ=0 EndX=-45.5062 EndY=78.819 EndZ=0
    g11: LineSegment StartX=-45.5062 StartY=78.819 StartZ=0 EndX=-91.0124 EndY=0 EndZ=0
    g12: LineSegment StartX=-91.0124 StartY=0 StartZ=0 EndX=-45.5062 EndY=-78.819 EndZ=0
  constraints (31):
    c: Coincident(g0,g1)
    c: Coincident(g1,g2)
    c: Coincident(g2,g3)
    c: Coincident(g3,g4)
    c: Coincident(g4,g5)
    c: Coincident(g5,g0)
    c: Equal(g0, g1-g5) x5
    c: PointOnObject(g0,g6)
    c: PointOnObject(g1,g6)
    c: PointOnObject(g2,g6)
    c: PointOnObject(g3,g6)
    c: PointOnObject(g4,g6)
    c: PointOnObject(g5,g6)
    c: Coincident(g6,g-1)
    c: Horizontal(g2)
    c: DistanceX(g3,g0) = 200.5
    c: Coincident(g7,g6)
    c: Coincident(g7,g2)
    c: Coincident(g8,g6)
    c: Coincident(g8,g4)
    c: Coincident(g9,g4)
    c: PointOnObject(g9,g8)
    c: Coincident(g10,g2)
    c: PointOnObject(g10,g7)
    c: Coincident(g11,g10)
    c: PointOnObject(g11,g-1)
    c: Coincident(g12,g11)
    c: Coincident(g12,g9)
    c: Parallel(g3,g11)
    c: Parallel(g12,g4)
    c: Distance(g11,g3) = 8
FEATURE [PartDesign::Pad] Pad002
  Direction = (0,0,1)
  Length = 3
  Length2 = 10
  Profile = -> Sketch002
  ReferenceAxis = -> Sketch002 [N_Axis]
  Refine = true
  SideType = 0
  Suppressed = false
  Type = 0
  Type2 = 0
  expr: Length = Spreadsheet.H2
FEATURE [Sketcher::SketchObject] Sketch003  label="Sketch006"
  ArcFitTolerance = 1e-06
  AttachmentSupport = -> [XY_Plane013]
  ExternalTypes = [0]
  FullyConstrained = true
  MakeInternals = false
  MapMode = 5
  _ExternalGeoVersion = 0
  expr: Constraints[19] = Spreadsheet.H7 + Spreadsheet.H6
  expr: Constraints[34] = Spreadsheet.H4
  sketch-geometry (13):
    g0: LineSegment [constr] StartX=50.125 StartY=-86.819 StartZ=0 EndX=100.25 EndY=-5.542e-13 EndZ=0
    g1: LineSegment [constr] StartX=100.25 StartY=-5.542e-13 StartZ=0 EndX=50.125 EndY=86.819 EndZ=0
    g2: LineSegment [constr] StartX=50.125 StartY=86.819 StartZ=0 EndX=-50.125 EndY=86.819 EndZ=0
    g3: LineSegment StartX=-50.125 StartY=86.819 StartZ=0 EndX=-100.25 EndY=1.705e-13 EndZ=0
    g4: LineSegment StartX=-100.25 StartY=1.705e-13 StartZ=0 EndX=-50.125 EndY=-86.819 EndZ=0
    g5: LineSegment [constr] StartX=-50.125 StartY=-86.819 StartZ=0 EndX=50.125 EndY=-86.819 EndZ=0
    g6: Circle [constr] CenterX=0 CenterY=0 CenterZ=0 NormalX=0 NormalY=0 NormalZ=1 AngleXU=0 Radius=100.25
    g7: LineSegment [constr] StartX=0 StartY=0 StartZ=0 EndX=-50.125 EndY=86.819 EndZ=0
    g8: LineSegment [constr] StartX=0 StartY=0 StartZ=0 EndX=-50.125 EndY=-86.819 EndZ=0
    g9: LineSegment StartX=-50.125 StartY=-86.819 StartZ=0 EndX=-53.0118 EndY=-91.819 EndZ=0
    g10: LineSegment StartX=-50.125 StartY=86.819 StartZ=0 EndX=-53.0118 EndY=91.819 EndZ=0
    g11: LineSegment StartX=-53.0118 StartY=91.819 StartZ=0 EndX=-106.024 EndY=0 EndZ=0
    g12: LineSegment StartX=-106.024 StartY=0 StartZ=0 EndX=-53.0118 EndY=-91.819 EndZ=0
  constraints (31):
    c: Coincident(g0,g1)
    c: Coincident(g1,g2)
    c: Coincident(g2,g3)
    c: Coincident(g3,g4)
    c: Coincident(g4,g5)
    c: Coincident(g5,g0)
    c: Equal(g0, g1-g5) x5
    c: PointOnObject(g0,g6)
    c: PointOnObject(g1,g6)
    c: PointOnObject(g2,g6)
    c: PointOnObject(g3,g6)
    c: PointOnObject(g4,g6)
    c: PointOnObject(g5,g6)
    c: Coincident(g6,g-1)
    c: Horizontal(g2)
    c: DistanceX(g3,g0) = 200.5
    c: Coincident(g7,g6)
    c: Coincident(g7,g2)
    c: Coincident(g8,g6)
    c: Coincident(g8,g4)
    c: Coincident(g9,g4)
    c: PointOnObject(g9,g8)
    c: Coincident(g10,g2)
    c: PointOnObject(g10,g7)
    c: Coincident(g11,g10)
    c: PointOnObject(g11,g-1)
    c: Coincident(g12,g11)
    c: Coincident(g12,g9)
    c: Parallel(g3,g11)
    c: Parallel(g12,g4)
    c: Distance(g3,g11) = 5
FEATURE [PartDesign::Pad] Pad003
  BaseFeature = -> Pad002
  Direction = (0,0,1)
  Length = 10.35
  Length2 = 10
  Profile = -> Sketch003
  ReferenceAxis = -> Sketch003 [N_Axis]
  Refine = true
  SideType = 0
  Suppressed = false
  Type = 0
  Type2 = 0
  expr: Length = Spreadsheet.H5
FEATURE [PartDesign::Fillet] Fillet001
  Base = -> Pad001 [Edge5,Edge8,Edge11,Edge14,Edge2,Edge1]
  BaseFeature = -> Pad001
  Radius = 1
  Refine = true
  SupportTransform = false
  Suppressed = false
  UseAllEdges = false
FEATURE [PartDesign::Body] Body001
  AllowCompound = false
  Group = -> [Pad001,Sketch,Fillet001]
  Origin = -> Origin011
  Placement = pos=(0,0,0) rot=(0,0,1;0.523599rad)
  Tip = -> Fillet001
FEATURE [App::Part] Part009  label="Mirror"
  Group = -> [Body001]
  Origin = -> Origin010
FEATURE [Sketcher::SketchObject] Sketch004  label="Sketch007"
  ArcFitTolerance = 1e-06
  AttachmentSupport = -> [XZ_Plane014]
  ExternalTypes = [0]
  FullyConstrained = true
  MakeInternals = false
  MapMode = 5
  Placement = pos=(0,0,0) rot=(1,0,0;1.5708rad)
  _ExternalGeoVersion = 0
  expr: Constraints[16] = Spreadsheet.H9
  expr: Constraints[17] = Spreadsheet.H12
  expr: Constraints[18] = Spreadsheet.H1 + Spreadsheet.H6
  expr: Constraints[7] = Spreadsheet.H10 / 2
  expr: Constraints[9] = Spreadsheet.H11
  sketch-geometry (7):
    g0: LineSegment StartX=-103.5 StartY=6.85 StartZ=0 EndX=-104 EndY=8.35 EndZ=0
    g1: LineSegment StartX=-104 StartY=8.35 StartZ=0 EndX=-103.5 EndY=9.85 EndZ=0
    g2: LineSegment StartX=-103.5 StartY=9.85 StartZ=0 EndX=-101.5 EndY=9.85 EndZ=0
    g3: LineSegment StartX=-101.5 StartY=9.85 StartZ=0 EndX=-101 EndY=8.35 EndZ=0
    g4: LineSegment StartX=-101 StartY=8.35 StartZ=0 EndX=-101.5 EndY=6.85 EndZ=0
    g5: LineSegment StartX=-101.5 StartY=6.85 StartZ=0 EndX=-103.5 EndY=6.85 EndZ=0
    g6: LineSegment [constr] StartX=-102.5 StartY=9.85 StartZ=0 EndX=-102.5 EndY=6.85 EndZ=0
  constraints (19):
    c: Coincident(g1,g0)
    c: Coincident(g2,g1)
    c: Coincident(g3,g2)
    c: Coincident(g5,g4)
    c: Coincident(g5,g0)
    c: Equal(g2,g5)
    c: Coincident(g3,g4)
    c: DistanceX(g0,g1) = 0.5
    c: Equal(g1,g0)
    c: DistanceX(g0,g3) = 3
    c: PointOnObject(g6,g2)
    c: Symmetric(g5,g5,g6)
    c: Vertical(g6)
    c: Symmetric(g1,g2,g6)
    c: Symmetric(g0,g3,g6)
    c: Horizontal(g5)
    c: DistanceY(g6,g6) = 3
    c: Distance(g-1,g6) = 102.5
    c: Distance(g-1,g5) = 6.85
FEATURE [Sketcher::SketchObject] Sketch005  label="Sketch008"
  ArcFitTolerance = 1e-06
  AttachmentSupport = -> [XY_Plane014]
  ExternalTypes = [0]
  FullyConstrained = true
  MakeInternals = false
  MapMode = 5
  _ExternalGeoVersion = 0
  expr: Constraints[4] = Spreadsheet.H7 / 1.5
  sketch-geometry (2):
    g0: LineSegment StartX=0 StartY=0 StartZ=0 EndX=66.6667 EndY=115.47 EndZ=0
    g1: LineSegment StartX=0 StartY=0 StartZ=0 EndX=66.6667 EndY=-115.47 EndZ=0
  constraints (5):
    c: Coincident(g0,g-1)
    c: Coincident(g1,g0)
    c: Symmetric(g0,g1,g-1)
    c: Angle(g1,g0) = 2.0944
    c: Distance(g1,g1) = 133.333
FEATURE [PartDesign::AdditivePipe] AdditivePipe
  AuxiliaryCurvilinear = true
  AuxiliarySpineTangent = false
  Binormal = (0,0,0)
  Mode = 0
  Placement = pos=(0,0,0) rot=(1,0,0;1.5708rad)
  Profile = -> Sketch004
  Refine = true
  Spine = -> Sketch005
  SpineTangent = false
  Suppressed = false
  Transformation = 0
  Transition = 0
FEATURE [Sketcher::SketchObject] Sketch006  label="Sketch009"
  ArcFitTolerance = 1e-06
  AttachmentSupport = -> [XY_Plane014]
  ExternalTypes = [0]
  FullyConstrained = true
  MakeInternals = false
  MapMode = 5
  _ExternalGeoVersion = 0
  expr: Constraints[18] = Spreadsheet.H7 * 1.5
  expr: Constraints[34] = Spreadsheet.H7
  sketch-geometry (13):
    g0: LineSegment [constr] StartX=75 StartY=-129.904 StartZ=0 EndX=150 EndY=0 EndZ=0
    g1: LineSegment [constr] StartX=150 StartY=0 StartZ=0 EndX=75 EndY=129.904 EndZ=0
    g2: LineSegment [constr] StartX=75 StartY=129.904 StartZ=0 EndX=-75 EndY=129.904 EndZ=0
    g3: LineSegment [constr] StartX=-75 StartY=129.904 StartZ=0 EndX=-150 EndY=-2.84e-14 EndZ=0
    g4: LineSegment [constr] StartX=-150 StartY=-2.84e-14 StartZ=0 EndX=-75 EndY=-129.904 EndZ=0
    g5: LineSegment [constr] StartX=-75 StartY=-129.904 StartZ=0 EndX=75 EndY=-129.904 EndZ=0
    g6: Circle [constr] CenterX=0 CenterY=0 CenterZ=0 NormalX=0 NormalY=0 NormalZ=1 AngleXU=0 Radius=150
    g7: LineSegment StartX=0 StartY=0 StartZ=0 EndX=-115.47 EndY=200 EndZ=0
    g8: LineSegment StartX=0 StartY=0 StartZ=0 EndX=-115.47 EndY=-200 EndZ=0
    g9: LineSegment StartX=-115.47 StartY=-200 StartZ=0 EndX=34.5299 EndY=-200 EndZ=0
    g10: LineSegment StartX=34.5299 StartY=-200 StartZ=0 EndX=150 EndY=0 EndZ=0
    g11: LineSegment StartX=-115.47 StartY=200 StartZ=0 EndX=34.5299 EndY=200 EndZ=0
    g12: LineSegment StartX=34.5299 StartY=200 StartZ=0 EndX=150 EndY=0 EndZ=0
  constraints (31):
    c: Coincident(g0,g1)
    c: Coincident(g1,g2)
    c: Coincident(g2,g3)
    c: Coincident(g3,g4)
    c: Coincident(g4,g5)
    c: Coincident(g5,g0)
    c: Equal(g0, g1-g5) x5
    c: PointOnObject(g0,g6)
    c: PointOnObject(g1,g6)
    c: PointOnObject(g3,g6)
    c: PointOnObject(g4,g6)
    c: PointOnObject(g5,g6)
    c: Coincident(g6,g-1)
    c: Horizontal(g2)
    c: Diameter(g6) = 300
    c: Coincident(g7,g6)
    c: Coincident(g8,g6)
    c: PointOnObject(g2,g7)
    c: PointOnObject(g2,g6)
    c: Coincident(g9,g8)
    c: Coincident(g10,g9)
    c: Coincident(g10,g0)
    c: Coincident(g12,g11)
    c: Coincident(g12,g0)
    c: Horizontal(g11)
    c: Horizontal(g9)
    c: Coincident(g11,g7)
    c: Parallel(g7,g12)
    c: Parallel(g8,g10)
    c: Symmetric(g7,g8,g-1)
    c: DistanceY(g7,g7) = 200
FEATURE [PartDesign::Pocket] Pocket
  BaseFeature = -> AdditivePipe
  Direction = (0,0,-1)
  Length = 100
  Length2 = 5
  Placement = pos=(0,0,0) rot=(1,0,0;1.5708rad)
  Profile = -> Sketch006
  ReferenceAxis = -> Sketch006 [N_Axis]
  Refine = true
  Reversed = true
  SideType = 0
  Suppressed = false
  Type = 0
  Type2 = 0
FEATURE [PartDesign::Fillet] Fillet002
  Base = -> Pocket [Edge12,Edge2,Edge28,Edge19]
  BaseFeature = -> Pocket
  Placement = pos=(0,0,0) rot=(1,0,0;1.5708rad)
  Radius = 1
  Refine = true
  SupportTransform = false
  Suppressed = false
  UseAllEdges = false
FEATURE [PartDesign::Body] Body003
  AllowCompound = false
  Group = -> [Sketch004,Sketch005,AdditivePipe,Sketch006,Pocket,Fillet002]
  Origin = -> Origin014
  Tip = -> Fillet002
FEATURE [PartDesign::SubShapeBinder] Binder
  BindCopyOnChange = 0
  BindMode = 0
  ClaimChildren = false
  Context = -> Part010 [Body002.Boolean.Binder.]
  Fuse = true
  MakeFace = true
  OffsetFill = false
  OffsetIntersection = false
  OffsetJoinType = 0
  OffsetOpenResult = false
  PartialLoad = false
  Refine = true
  Relative = true
  Support = -> [Body003]
  _Version = 2
FEATURE [PartDesign::Boolean] Boolean
  BaseFeature = -> Pad003
  Group = -> [Binder]
  Refine = true
  Suppressed = false
  Type = 0
FEATURE [Sketcher::SketchObject] Sketch007  label="Sketch010"
  ArcFitTolerance = 1e-06
  AttachmentSupport = -> [XY_Plane013]
  ExternalTypes = [0]
  FullyConstrained = true
  MakeInternals = false
  MapMode = 5
  _ExternalGeoVersion = 0
  expr: Constraints[19] = Spreadsheet.H7 + Spreadsheet.H6
  expr: Constraints[36] = Spreadsheet.H14
  expr: Constraints[37] = Spreadsheet.H14
  expr: Constraints[52] = Spreadsheet.H4
  sketch-geometry (19):
    g0: LineSegment [constr] StartX=50.125 StartY=86.819 StartZ=0 EndX=-50.125 EndY=86.819 EndZ=0
    g1: LineSegment [constr] StartX=-50.125 StartY=86.819 StartZ=0 EndX=-100.25 EndY=0 EndZ=0
    g2: LineSegment [constr] StartX=-100.25 StartY=0 StartZ=0 EndX=-50.125 EndY=-86.819 EndZ=0
    g3: LineSegment [constr] StartX=-50.125 StartY=-86.819 StartZ=0 EndX=50.125 EndY=-86.819 EndZ=0
    g4: LineSegment [constr] StartX=50.125 StartY=-86.819 StartZ=0 EndX=100.25 EndY=-1.42e-14 EndZ=0
    g5: LineSegment [constr] StartX=100.25 StartY=-1.42e-14 StartZ=0 EndX=50.125 EndY=86.819 EndZ=0
    g6: Circle [constr] CenterX=0 CenterY=0 CenterZ=0 NormalX=0 NormalY=0 NormalZ=1 AngleXU=0 Radius=100.25
    g7: LineSegment [constr] StartX=0 StartY=0 StartZ=0 EndX=-53.0118 EndY=91.819 EndZ=0
    g8: LineSegment [constr] StartX=1.588e-13 StartY=0 StartZ=0 EndX=-53.0118 EndY=-91.819 EndZ=0
    g9: LineSegment [constr] StartX=-53.0118 StartY=91.819 StartZ=0 EndX=-106.024 EndY=0 EndZ=0
    g10: LineSegment [constr] StartX=-106.024 StartY=0 StartZ=0 EndX=-53.0118 EndY=-91.819 EndZ=0
    g11: LineSegment StartX=-61.9551 StartY=76.3287 StartZ=0 EndX=-57.625 EndY=73.8287 EndZ=0
    g12: LineSegment StartX=-97.0801 StartY=15.4904 StartZ=0 EndX=-92.75 EndY=12.9904 EndZ=0
    g13: LineSegment StartX=-97.0801 StartY=-15.4904 StartZ=0 EndX=-92.75 EndY=-12.9904 EndZ=0
    g14: LineSegment StartX=-61.9551 StartY=-76.3287 StartZ=0 EndX=-57.625 EndY=-73.8287 EndZ=0
    g15: LineSegment StartX=-57.625 StartY=73.8287 StartZ=0 EndX=-92.75 EndY=12.9904 EndZ=0
    g16: LineSegment StartX=-97.0801 StartY=15.4904 StartZ=0 EndX=-61.9551 EndY=76.3287 EndZ=0
    g17: LineSegment StartX=-92.75 StartY=-12.9904 StartZ=0 EndX=-57.625 EndY=-73.8287 EndZ=0
    g18: LineSegment StartX=-61.9551 StartY=-76.3287 StartZ=0 EndX=-97.0801 EndY=-15.4904 EndZ=0
  constraints (49):
    c: Coincident(g0,g1)
    c: Coincident(g1,g2)
    c: Coincident(g2,g3)
    c: Coincident(g3,g4)
    c: Coincident(g4,g5)
    c: Coincident(g5,g0)
    c: Equal(g0, g1-g5) x5
    c: PointOnObject(g0,g6)
    c: PointOnObject(g1,g6)
    c: PointOnObject(g2,g6)
    c: PointOnObject(g3,g6)
    c: PointOnObject(g4,g6)
    c: PointOnObject(g5,g6)
    c: Coincident(g6,g-1)
    c: Horizontal(g0)
    c: Diameter(g6) = 200.5
    c: Coincident(g7,g6)
    c: PointOnObject(g8,g-1)
    c: PointOnObject(g2,g8)
    c: PointOnObject(g0,g7)
    c: Symmetric(g7,g8,g-1)
    c: Coincident(g9,g7)
    c: PointOnObject(g9,g-1)
    c: Coincident(g10,g9)
    c: Coincident(g10,g8)
    c: Parallel(g10,g2)
    c: PointOnObject(g11,g9)
    c: PointOnObject(g11,g1)
    c: PointOnObject(g12,g9)
    c: PointOnObject(g12,g1)
    c: Perpendicular(g11,g9)
    c: Perpendicular(g12,g9)
    c: Distance(g0,g11) = 15
    c: Distance(g12,g1) = 15
    c: PointOnObject(g13,g10)
    c: PointOnObject(g14,g10)
    c: Perpendicular(g13,g2)
    c: Perpendicular(g14,g2)
    c: Symmetric(g12,g13,g-1)
    c: Symmetric(g14,g11,g-1)
    c: Coincident(g15,g11)
    c: Coincident(g15,g12)
    c: Coincident(g16,g12)
    c: Coincident(g16,g11)
    c: Coincident(g17,g13)
    c: Coincident(g17,g14)
    c: Coincident(g18,g14)
    c: Coincident(g18,g13)
    c: Distance(g1,g9) = 5
FEATURE [PartDesign::Pocket] Pocket001
  BaseFeature = -> Boolean
  Direction = (0,0,-1)
  Length = 100
  Length2 = 5
  Profile = -> Sketch007
  ReferenceAxis = -> Sketch007 [N_Axis]
  Refine = true
  Reversed = true
  SideType = 0
  Suppressed = false
  Type = 0
  Type2 = 0
FEATURE [Sketcher::SketchObject] Sketch008  label="Sketch011"
  ArcFitTolerance = 1e-06
  AttachmentSupport = -> [XY_Plane013]
  ExternalTypes = [0]
  FullyConstrained = true
  MakeInternals = false
  MapMode = 5
  _ExternalGeoVersion = 0
  expr: Constraints[19] = Spreadsheet.H7 + Spreadsheet.H6
  expr: Constraints[23] = Spreadsheet.H4
  expr: Constraints[33] = Spreadsheet.H4
  expr: Constraints[34] = Spreadsheet.H19
  sketch-geometry (15):
    g0: LineSegment [constr] StartX=50.125 StartY=86.819 StartZ=0 EndX=-50.125 EndY=86.819 EndZ=0
    g1: LineSegment [constr] StartX=-50.125 StartY=86.819 StartZ=0 EndX=-100.25 EndY=0 EndZ=0
    g2: LineSegment [constr] StartX=-100.25 StartY=0 StartZ=0 EndX=-50.125 EndY=-86.819 EndZ=0
    g3: LineSegment [constr] StartX=-50.125 StartY=-86.819 StartZ=0 EndX=50.125 EndY=-86.819 EndZ=0
    g4: LineSegment [constr] StartX=50.125 StartY=-86.819 StartZ=0 EndX=100.25 EndY=0 EndZ=0
    g5: LineSegment [constr] StartX=100.25 StartY=0 StartZ=0 EndX=50.125 EndY=86.819 EndZ=0
    g6: Circle [constr] CenterX=0 CenterY=0 CenterZ=0 NormalX=0 NormalY=0 NormalZ=1 AngleXU=0 Radius=100.25
    g7: LineSegment StartX=-88.3301 StartY=-30.6458 StartZ=0 EndX=-90.8301 EndY=-26.3157 EndZ=0
    g8: LineSegment StartX=-90.8301 StartY=-26.3157 StartZ=0 EndX=-86.5 EndY=-23.8157 EndZ=0
    g9: LineSegment StartX=-86.5 StartY=23.8157 StartZ=0 EndX=-84 EndY=28.1458 EndZ=0
    g10: LineSegment StartX=-84 StartY=28.1458 StartZ=0 EndX=-88.3301 EndY=30.6458 EndZ=0
    g11: LineSegment StartX=-88.3301 StartY=30.6458 StartZ=0 EndX=-90.8301 EndY=26.3157 EndZ=0
    g12: LineSegment StartX=-90.8301 StartY=26.3157 StartZ=0 EndX=-86.5 EndY=23.8157 EndZ=0
    g13: LineSegment StartX=-86.5 StartY=-23.8157 StartZ=0 EndX=-84 EndY=-28.1458 EndZ=0
    g14: LineSegment StartX=-88.3301 StartY=-30.6458 StartZ=0 EndX=-84 EndY=-28.1458 EndZ=0
  constraints (39):
    c: Coincident(g0,g1)
    c: Coincident(g1,g2)
    c: Coincident(g2,g3)
    c: Coincident(g3,g4)
    c: Coincident(g4,g5)
    c: Coincident(g5,g0)
    c: Equal(g0, g1-g5) x5
    c: PointOnObject(g0,g6)
    c: PointOnObject(g1,g6)
    c: PointOnObject(g2,g6)
    c: PointOnObject(g3,g6)
    c: PointOnObject(g4,g6)
    c: PointOnObject(g5,g6)
    c: Coincident(g6,g-1)
    c: Horizontal(g0)
    c: Diameter(g6) = 200.5
    c: PointOnObject(g8,g2)
    c: Coincident(g8,g7)
    c: Equal(g8,g7)
    c: Distance(g8,g8) = 5
    c: PointOnObject(g9,g1)
    c: Coincident(g10,g9)
    c: Coincident(g11,g10)
    c: Coincident(g12,g11)
    c: Coincident(g12,g9)
    c: Perpendicular(g10,g11)
    c: Perpendicular(g12,g11)
    c: Equal(g11,g10)
    c: Equal(g11,g12)
    c: Distance(g10,g10) = 5
    c: Distance(g1,g8) = 27.5
    c: Coincident(g13,g8)
    c: Coincident(g14,g7)
    c: Coincident(g14,g13)
    c: PointOnObject(g13,g2)
    c: Equal(g13,g7)
    c: Equal(g8,g14)
    c: Perpendicular(g7,g8)
    c: Symmetric(g9,g8,g-1)
FEATURE [PartDesign::Pad] Pad004
  BaseFeature = -> Pocket001
  Direction = (0,0,1)
  Length = 10.35
  Length2 = 10
  Profile = -> Sketch008
  ReferenceAxis = -> Sketch008 [N_Axis]
  Refine = true
  SideType = 0
  Suppressed = false
  Type = 0
  Type2 = 0
  expr: Length = Spreadsheet.H5
FEATURE [Sketcher::SketchObject] Sketch009  label="Sketch012"
  ArcFitTolerance = 1e-06
  AttachmentSupport = -> [XY_Plane013]
  ExternalTypes = [0]
  FullyConstrained = true
  MakeInternals = false
  MapMode = 5
  _ExternalGeoVersion = 0
  expr: Constraints[1] = Spreadsheet.H20 - Spreadsheet.H21
  expr: Constraints[22] = Spreadsheet.H7 + Spreadsheet.H6
  expr: Constraints[26] = Spreadsheet.H4 / 2
  expr: Constraints[27] = Spreadsheet.H18
  sketch-geometry (10):
    g0: Circle CenterX=-87.4151 CenterY=27.2308 CenterZ=0 NormalX=0 NormalY=0 NormalZ=1 AngleXU=0 Radius=1.25
    g1: Circle CenterX=-87.4151 CenterY=-27.2308 CenterZ=0 NormalX=0 NormalY=0 NormalZ=1 AngleXU=0 Radius=1.25
    g2: LineSegment [constr] StartX=-50.125 StartY=86.819 StartZ=0 EndX=-100.25 EndY=0 EndZ=0
    g3: LineSegment [constr] StartX=-100.25 StartY=0 StartZ=0 EndX=-50.125 EndY=-86.819 EndZ=0
    g4: LineSegment [constr] StartX=-50.125 StartY=-86.819 StartZ=0 EndX=50.125 EndY=-86.819 EndZ=0
    g5: LineSegment [constr] StartX=50.125 StartY=-86.819 StartZ=0 EndX=100.25 EndY=0 EndZ=0
    g6: LineSegment [constr] StartX=100.25 StartY=0 StartZ=0 EndX=50.125 EndY=86.819 EndZ=0
    g7: LineSegment [constr] StartX=50.125 StartY=86.819 StartZ=0 EndX=-50.125 EndY=86.819 EndZ=0
    g8: Circle [constr] CenterX=0 CenterY=0 CenterZ=0 NormalX=0 NormalY=0 NormalZ=1 AngleXU=0 Radius=100.25
    g9: LineSegment [constr] StartX=-87.4151 StartY=-27.2308 StartZ=0 EndX=-85.25 EndY=-25.9808 EndZ=0
  constraints (24):
    c: Equal(g0,g1)
    c: Diameter(g0) = 2.5
    c: Symmetric(g0,g1,g-1)
    c: Coincident(g2,g3)
    c: Coincident(g3,g4)
    c: Coincident(g4,g5)
    c: Coincident(g5,g6)
    c: Coincident(g6,g7)
    c: Coincident(g7,g2)
    c: Equal(g2, g3-g7) x5
    c: PointOnObject(g2,g8)
    c: PointOnObject(g3,g8)
    c: PointOnObject(g4,g8)
    c: PointOnObject(g5,g8)
    c: PointOnObject(g6,g8)
    c: PointOnObject(g7,g8)
    c: Coincident(g8,g-1)
    c: Horizontal(g7)
    c: Diameter(g8) = 200.5
    c: Coincident(g9,g1)
    c: PointOnObject(g9,g3)
    c: Perpendicular(g9,g3)
    c: Distance(g9,g9) = 2.5
    c: Distance(g9,g2) = 30
FEATURE [PartDesign::Pad] Pad005
  BaseFeature = -> Pad004
  Direction = (0,0,1)
  Length = 13.35
  Length2 = 10
  Profile = -> Sketch009
  ReferenceAxis = -> Sketch009 [N_Axis]
  Refine = true
  SideType = 0
  Suppressed = false
  Type = 0
  Type2 = 0
  expr: Length = Spreadsheet.K9
FEATURE [PartDesign::Plane] DatumPlane
  Length = 160.897
  MapMode = 1
  Placement = pos=(0,0,6.85) rot=(0,0,1;0rad)
  ResizeMode = 0
  Width = 212.388
  expr: .Placement.Base.z = Spreadsheet.H5 - Spreadsheet.H2 - Spreadsheet.H6
FEATURE [Sketcher::SketchObject] Sketch010  label="Sketch013"
  ArcFitTolerance = 1e-06
  AttachmentSupport = -> [DatumPlane]
  ExternalTypes = [0]
  FullyConstrained = true
  MakeInternals = false
  MapMode = 5
  Placement = pos=(0,0,6.85) rot=(0,0,1;0rad)
  _ExternalGeoVersion = 0
  expr: Constraints[19] = Spreadsheet.H7 + Spreadsheet.H6
  expr: Constraints[28] = Spreadsheet.H4
  expr: Constraints[40] = Spreadsheet.H3
  sketch-geometry (15):
    g0: LineSegment [constr] StartX=50.125 StartY=86.819 StartZ=0 EndX=-50.125 EndY=86.819 EndZ=0
    g1: LineSegment [constr] StartX=-50.125 StartY=86.819 StartZ=0 EndX=-100.25 EndY=0 EndZ=0
    g2: LineSegment [constr] StartX=-100.25 StartY=0 StartZ=0 EndX=-50.125 EndY=-86.819 EndZ=0
    g3: LineSegment [constr] StartX=-50.125 StartY=-86.819 StartZ=0 EndX=50.125 EndY=-86.819 EndZ=0
    g4: LineSegment [constr] StartX=50.125 StartY=-86.819 StartZ=0 EndX=100.25 EndY=0 EndZ=0
    g5: LineSegment [constr] StartX=100.25 StartY=0 StartZ=0 EndX=50.125 EndY=86.819 EndZ=0
    g6: Circle [constr] CenterX=0 CenterY=0 CenterZ=0 NormalX=0 NormalY=0 NormalZ=1 AngleXU=0 Radius=100.25
    g7: LineSegment [constr] StartX=0 StartY=0 StartZ=0 EndX=-53.0118 EndY=91.819 EndZ=0
    g8: LineSegment [constr] StartX=0 StartY=0 StartZ=0 EndX=-53.0118 EndY=-91.819 EndZ=0
    g9: LineSegment StartX=-53.0118 StartY=-91.819 StartZ=0 EndX=-106.024 EndY=0 EndZ=0
    g10: LineSegment StartX=-106.024 StartY=0 StartZ=0 EndX=-53.0118 EndY=91.819 EndZ=0
    g11: LineSegment StartX=-53.0118 StartY=91.819 StartZ=0 EndX=-45.5062 EndY=78.819 EndZ=0
    g12: LineSegment StartX=-53.0118 StartY=-91.819 StartZ=0 EndX=-45.5062 EndY=-78.819 EndZ=0
    g13: LineSegment StartX=-45.5062 StartY=-78.819 StartZ=0 EndX=-91.0124 EndY=0 EndZ=0
    g14: LineSegment StartX=-45.5062 StartY=78.819 StartZ=0 EndX=-91.0124 EndY=0 EndZ=0
  constraints (37):
    c: Coincident(g0,g1)
    c: Coincident(g1,g2)
    c: Coincident(g2,g3)
    c: Coincident(g3,g4)
    c: Coincident(g4,g5)
    c: Coincident(g5,g0)
    c: Equal(g0, g1-g5) x5
    c: PointOnObject(g0,g6)
    c: PointOnObject(g1,g6)
    c: PointOnObject(g2,g6)
    c: PointOnObject(g3,g6)
    c: PointOnObject(g4,g6)
    c: PointOnObject(g5,g6)
    c: Coincident(g6,g-1)
    c: Horizontal(g0)
    c: Diameter(g6) = 200.5
    c: Coincident(g7,g6)
    c: PointOnObject(g0,g7)
    c: Coincident(g8,g6)
    c: PointOnObject(g2,g8)
    c: Coincident(g9,g8)
    c: Coincident(g10,g9)
    c: Coincident(g10,g7)
    c: PointOnObject(g9,g-1)
    c: Distance(g0,g10) = 5
    c: Coincident(g11,g7)
    c: PointOnObject(g11,g7)
    c: Coincident(g12,g8)
    c: Coincident(g13,g12)
    c: PointOnObject(g13,g-1)
    c: Coincident(g14,g11)
    c: Coincident(g14,g13)
    c: Parallel(g10,g14)
    c: Parallel(g13,g9)
    c: Parallel(g2,g9)
    c: Symmetric(g11,g12,g-1)
    c: Distance(g14,g1) = 8
FEATURE [PartDesign::Pad] Pad006
  Direction = (0,0,1)
  Length = 3
  Length2 = 10
  Placement = pos=(0,0,6.85) rot=(0,0,1;0rad)
  Profile = -> Sketch010
  ReferenceAxis = -> Sketch010 [N_Axis]
  Refine = true
  SideType = 0
  Suppressed = false
  Type = 0
  Type2 = 0
  expr: Length = Spreadsheet.H11
FEATURE [PartDesign::SubShapeBinder] Binder001
  BindCopyOnChange = 0
  BindMode = 0
  ClaimChildren = false
  Context = -> Part010 [Body004.Binder001.]
  Fuse = false
  MakeFace = true
  OffsetFill = false
  OffsetIntersection = false
  OffsetJoinType = 0
  OffsetOpenResult = false
  PartialLoad = false
  Refine = true
  Relative = true
  Support = -> [Body003]
  _Version = 2
FEATURE [PartDesign::Boolean] Boolean001
  BaseFeature = -> Pad006
  Group = -> [Binder001]
  Refine = true
  Suppressed = false
  Type = 1
FEATURE [PartDesign::Fillet] Fillet
  Base = -> Pad005 [Edge36,Edge37,Edge34,Edge33,Edge119,Edge120,Edge116,Edge117,Edge47,Edge45,Edge51,Edge53,Edge109,Edge110,Edge107,Edge106,Edge70,Edge71,Edge68,Edge67,Edge14,Edge15,Edge12,Edge11]
  BaseFeature = -> Pad005
  Radius = 0.5
  Refine = true
  SupportTransform = false
  Suppressed = false
  UseAllEdges = false
FEATURE [PartDesign::Fillet] Fillet004
  Base = -> Fillet [Edge146,Edge145,Edge159,Edge158,Edge148,Edge76,Edge128,Edge133,Edge130,Edge127,Edge124,Edge114,Edge112,Edge110,Edge109,Edge91,Edge94,Edge92,Edge97,Edge41,Edge43,Edge14,Edge11,Edge10]
  BaseFeature = -> Fillet
  Radius = 1
  Refine = true
  SupportTransform = false
  Suppressed = false
  UseAllEdges = false
FEATURE [PartDesign::Fillet] Fillet005
  Base = -> Fillet004 [Edge150,Edge184,Edge179,Edge185,Edge199,Edge155]
  BaseFeature = -> Fillet004
  Radius = 1
  Refine = true
  SupportTransform = false
  Suppressed = false
  UseAllEdges = false
FEATURE [PartDesign::Body] Body002
  AllowCompound = false
  Group = -> [Sketch002,Pad002,Sketch003,Pad003,Boolean,Sketch007,Pocket001,Sketch008,Pad004,Sketch009,Pad005,Fillet,Fillet004,Fillet005]
  Origin = -> Origin013
  Placement = pos=(0,0,-3.5) rot=(0,0,1;0rad)
  Tip = -> Fillet005
  expr: .Placement.Base.z = -Spreadsheet.H2 - Spreadsheet.H6
FEATURE [Sketcher::SketchObject] Sketch011  label="Sketch014"
  ArcFitTolerance = 1e-06
  AttachmentSupport = -> [DatumPlane]
  ExternalTypes = [0]
  FullyConstrained = true
  MakeInternals = false
  MapMode = 5
  Placement = pos=(0,0,6.85) rot=(0,0,1;0rad)
  _ExternalGeoVersion = 0
  expr: Constraints[17] = Spreadsheet.H7 + Spreadsheet.H6
  expr: Constraints[27] = Spreadsheet.H4
  expr: Constraints[28] = Spreadsheet.H16
  expr: Constraints[29] = Spreadsheet.H16
  sketch-geometry (15):
    g0: LineSegment [constr] StartX=50.125 StartY=86.819 StartZ=0 EndX=-50.125 EndY=86.819 EndZ=0
    g1: LineSegment [constr] StartX=-50.125 StartY=86.819 StartZ=0 EndX=-100.25 EndY=1.42e-14 EndZ=0
    g2: LineSegment [constr] StartX=-100.25 StartY=1.42e-14 StartZ=0 EndX=-50.125 EndY=-86.819 EndZ=0
    g3: LineSegment [constr] StartX=-50.125 StartY=-86.819 StartZ=0 EndX=50.125 EndY=-86.819 EndZ=0
    g4: LineSegment [constr] StartX=50.125 StartY=-86.819 StartZ=0 EndX=100.25 EndY=0 EndZ=0
    g5: LineSegment [constr] StartX=100.25 StartY=0 StartZ=0 EndX=50.125 EndY=86.819 EndZ=0
    g6: Circle [constr] CenterX=0 CenterY=0 CenterZ=0 NormalX=0 NormalY=0 NormalZ=1 AngleXU=0 Radius=100.25
    g7: LineSegment StartX=-87.75 StartY=21.6506 StartZ=0 EndX=-62.625 EndY=65.1684 EndZ=0
    g8: LineSegment StartX=-62.625 StartY=65.1684 StartZ=0 EndX=-66.9551 EndY=67.6684 EndZ=0
    g9: LineSegment StartX=-87.75 StartY=21.6506 StartZ=0 EndX=-92.0801 EndY=24.1506 EndZ=0
    g10: LineSegment StartX=-92.0801 StartY=24.1506 StartZ=0 EndX=-66.9551 EndY=67.6684 EndZ=0
    g11: LineSegment StartX=-87.75 StartY=-21.6506 StartZ=0 EndX=-62.625 EndY=-65.1684 EndZ=0
    g12: LineSegment StartX=-62.625 StartY=-65.1684 StartZ=0 EndX=-66.9551 EndY=-67.6684 EndZ=0
    g13: LineSegment StartX=-66.9551 StartY=-67.6684 StartZ=0 EndX=-92.0801 EndY=-24.1506 EndZ=0
    g14: LineSegment StartX=-92.0801 StartY=-24.1506 StartZ=0 EndX=-87.75 EndY=-21.6506 EndZ=0
  constraints (39):
    c: Coincident(g0,g1)
    c: Coincident(g1,g2)
    c: Coincident(g3,g4)
    c: Coincident(g4,g5)
    c: Coincident(g5,g0)
    c: Equal(g0, g1-g5) x5
    c: PointOnObject(g0,g6)
    c: PointOnObject(g1,g6)
    c: PointOnObject(g2,g6)
    c: PointOnObject(g3,g6)
    c: PointOnObject(g4,g6)
    c: PointOnObject(g5,g6)
    c: Horizontal(g0)
    c: Diameter(g6) = 200.5
    c: PointOnObject(g7,g1)
    c: PointOnObject(g7,g1)
    c: Coincident(g8,g7)
    c: Coincident(g9,g7)
    c: Coincident(g10,g9)
    c: Coincident(g10,g8)
    c: Equal(g8,g9)
    c: Perpendicular(g7,g8)
    c: Perpendicular(g7,g9)
    c: Distance(g8,g8) = 5
    c: Distance(g7,g0) = 25
    c: Distance(g1,g7) = 25
    c: PointOnObject(g11,g2)
    c: Coincident(g12,g11)
    c: Coincident(g13,g12)
    c: Coincident(g14,g11)
    c: Perpendicular(g11,g14)
    c: Perpendicular(g11,g12)
    c: Equal(g14,g9)
    c: Coincident(g14,g13)
    c: Perpendicular(g12,g13)
    c: Symmetric(g7,g11,g-1)
    c: Equal(g10,g13)
    c: Coincident(g2,g3)
    c: Coincident(g6,g-1)
FEATURE [PartDesign::Pad] Pad007
  BaseFeature = -> Boolean001
  Direction = (0,0,1)
  Length = 3
  Length2 = 10
  Profile = -> Sketch011
  ReferenceAxis = -> Sketch011 [N_Axis]
  Refine = true
  SideType = 0
  Suppressed = false
  Type = 0
  Type2 = 0
  expr: Length = Spreadsheet.H20
FEATURE [Sketcher::SketchObject] Sketch012  label="Sketch015"
  ArcFitTolerance = 1e-06
  AttachmentSupport = -> [DatumPlane]
  ExternalTypes = [0]
  FullyConstrained = true
  MakeInternals = false
  MapMode = 5
  Placement = pos=(0,0,6.85) rot=(0,0,1;0rad)
  _ExternalGeoVersion = 0
  expr: Constraints[19] = Spreadsheet.H7 + Spreadsheet.H6
  expr: Constraints[22] = Spreadsheet.H18
  expr: Constraints[23] = Spreadsheet.H4 / 2
  expr: Constraints[25] = Spreadsheet.H20
  expr: Constraints[36] = Spreadsheet.H23
  expr: Constraints[38] = Spreadsheet.I12
  sketch-geometry (14):
    g0: LineSegment [constr] StartX=50.125 StartY=86.819 StartZ=0 EndX=-50.125 EndY=86.819 EndZ=0
    g1: LineSegment [constr] StartX=-50.125 StartY=86.819 StartZ=0 EndX=-100.25 EndY=-1.42e-14 EndZ=0
    g2: LineSegment [constr] StartX=-100.25 StartY=-1.42e-14 StartZ=0 EndX=-50.125 EndY=-86.819 EndZ=0
    g3: LineSegment [constr] StartX=-50.125 StartY=-86.819 StartZ=0 EndX=50.125 EndY=-86.819 EndZ=0
    g4: LineSegment [constr] StartX=50.125 StartY=-86.819 StartZ=0 EndX=100.25 EndY=1.42e-14 EndZ=0
    g5: LineSegment [constr] StartX=100.25 StartY=1.42e-14 StartZ=0 EndX=50.125 EndY=86.819 EndZ=0
    g6: Circle [constr] CenterX=0 CenterY=0 CenterZ=0 NormalX=0 NormalY=0 NormalZ=1 AngleXU=0 Radius=100.25
    g7: LineSegment [constr] StartX=-65.125 StartY=60.8383 StartZ=0 EndX=-67.2901 EndY=62.0883 EndZ=0
    g8: Circle CenterX=-67.2901 CenterY=62.0883 CenterZ=0 NormalX=0 NormalY=0 NormalZ=1 AngleXU=0 Radius=1.5
    g9: Circle CenterX=-67.2901 CenterY=-62.0883 CenterZ=0 NormalX=0 NormalY=0 NormalZ=1 AngleXU=0 Radius=1.5
    g10: LineSegment StartX=-112.75 StartY=0.25 StartZ=0 EndX=-112.75 EndY=-0.25 EndZ=0
    g11: LineSegment StartX=-112.75 StartY=-0.25 StartZ=0 EndX=-102.75 EndY=-0.25 EndZ=0
    g12: LineSegment StartX=-102.75 StartY=-0.25 StartZ=0 EndX=-102.75 EndY=0.25 EndZ=0
    g13: LineSegment StartX=-102.75 StartY=0.25 StartZ=0 EndX=-112.75 EndY=0.25 EndZ=0
  constraints (35):
    c: Coincident(g0,g1)
    c: Coincident(g1,g2)
    c: Coincident(g2,g3)
    c: Coincident(g3,g4)
    c: Coincident(g4,g5)
    c: Coincident(g5,g0)
    c: Equal(g0, g1-g5) x5
    c: PointOnObject(g0,g6)
    c: PointOnObject(g1,g6)
    c: PointOnObject(g2,g6)
    c: PointOnObject(g3,g6)
    c: PointOnObject(g4,g6)
    c: PointOnObject(g5,g6)
    c: Coincident(g6,g-1)
    c: Horizontal(g0)
    c: Diameter(g6) = 200.5
    c: PointOnObject(g7,g1)
    c: Perpendicular(g1,g7)
    c: Distance(g0,g7) = 30
    c: Distance(g7,g7) = 2.5
    c: Coincident(g8,g7)
    c: Diameter(g8) = 3
    c: Symmetric(g7,g9,g-1)
    c: Equal(g8,g9)
    c: Coincident(g10,g11)
    c: Coincident(g11,g12)
    c: Coincident(g12,g13)
    c: Coincident(g13,g10)
    c: Vertical(g12)
    c: Horizontal(g11)
    c: Horizontal(g13)
    c: Symmetric(g10,g10,g-1)
    c: DistanceY(g10,g10) = 0.5
    c: DistanceX(g13,g13) = 10
    c: Distance(g1,g12) = 2.5
FEATURE [PartDesign::Pocket] Pocket002
  BaseFeature = -> Pad007
  Direction = (0,0,-1)
  Length = 100
  Length2 = 5
  Profile = -> Sketch012
  ReferenceAxis = -> Sketch012 [N_Axis]
  Refine = true
  Reversed = true
  SideType = 0
  Suppressed = false
  Type = 0
  Type2 = 0
FEATURE [Sketcher::SketchObject] Sketch013  label="Sketch016"
  ArcFitTolerance = 1e-06
  AttachmentSupport = -> [XZ_Plane015]
  ExternalTypes = [0]
  FullyConstrained = true
  MakeInternals = false
  MapMode = 5
  Placement = pos=(0,0,0) rot=(1,0,0;1.5708rad)
  _ExternalGeoVersion = 0
  expr: Constraints[3] = Spreadsheet.H9
  expr: Constraints[4] = Spreadsheet.H3 * 1 / cos(30)
  expr: Constraints[7] = Spreadsheet.H5 - Spreadsheet.H2 - Spreadsheet.H6
  expr: Constraints[8] = Spreadsheet.H7 / 2 + Spreadsheet.H6 / 2
  sketch-geometry (3):
    g0: LineSegment StartX=-91.0124 StartY=6.85 StartZ=0 EndX=-100.25 EndY=9.85 EndZ=0
    g1: LineSegment StartX=-100.25 StartY=9.85 StartZ=0 EndX=-91.0124 EndY=9.85 EndZ=0
    g2: LineSegment StartX=-91.0124 StartY=9.85 StartZ=0 EndX=-91.0124 EndY=6.85 EndZ=0
  constraints (9):
    c: Horizontal(g1)
    c: Coincident(g2,g0)
    c: Vertical(g2)
    c: DistanceY(g2,g2) = 3
    c: DistanceX(g1,g1) = 9.2376
    c: Coincident(g1,g2)
    c: Coincident(g0,g1)
    c: Distance(g0,g-1) = 6.85
    c: Distance(g0,g-2) = 100.25
FEATURE [PartDesign::SubtractivePipe] SubtractivePipe
  AuxiliaryCurvilinear = true
  AuxiliarySpineTangent = false
  BaseFeature = -> Pocket002
  Binormal = (0,0,0)
  Mode = 0
  Profile = -> Sketch013
  Refine = true
  Spine = -> Pocket002 [Edge36]
  SpineTangent = false
  Suppressed = false
  Transformation = 0
  Transition = 0
FEATURE [PartDesign::SubtractivePipe] SubtractivePipe001
  AuxiliaryCurvilinear = true
  AuxiliarySpineTangent = false
  BaseFeature = -> SubtractivePipe
  Binormal = (0,0,0)
  Mode = 0
  Profile = -> Sketch013
  Refine = true
  Spine = -> SubtractivePipe [Edge48]
  SpineTangent = false
  Suppressed = false
  Transformation = 0
  Transition = 0
FEATURE [PartDesign::Fillet] Fillet006
  Base = -> SubtractivePipe001 [Edge5,Edge61,Edge81,Edge80,Edge69,Edge68,Edge66]
  BaseFeature = -> SubtractivePipe001
  Radius = 1
  Refine = true
  SupportTransform = false
  Suppressed = false
  UseAllEdges = false
FEATURE [PartDesign::Body] Body004
  AllowCompound = true
  Group = -> [DatumPlane,Sketch010,Pad006,Boolean001,Sketch011,Pad007,Sketch012,Pocket002,Sketch013,SubtractivePipe,SubtractivePipe001,Fillet006]
  Origin = -> Origin015
  Tip = -> Fillet006
FEATURE [App::Part] Part010  label="Mirror frame"
  Group = -> [Body002,Body003,Body004]
  Origin = -> Origin012
FEATURE [PartDesign::SubShapeBinder] Binder002
  BindCopyOnChange = 0
  BindMode = 0
  ClaimChildren = false
  Context = -> Part011 [Body005.Binder002.]
  Fuse = false
  MakeFace = true
  OffsetFill = false
  OffsetIntersection = false
  OffsetJoinType = 0
  OffsetOpenResult = false
  PartialLoad = false
  Placement = pos=(-150,130,-85) rot=(0.31254,0.821685,-0.476605;1.35525rad)
  Refine = true
  Relative = true
  Support = -> [Part009[Body001.]]
  _Version = 2
FEATURE [PartDesign::Plane] DatumPlane001
  Length = 270
  MapMode = 1
  Placement = pos=(0,0,-170) rot=(0,0,1;0rad)
  ResizeMode = 0
  Width = 270
  expr: .Placement.Base.z = -Spreadsheet.B14 + Spreadsheet.E1
FEATURE [Sketcher::SketchObject] Sketch014  label="Sketch017"
  ArcFitTolerance = 1e-06
  AttachmentSupport = -> [DatumPlane001]
  ExternalGeometry = -> [Binder002]
  ExternalTypes = [0]
  FullyConstrained = true
  MakeInternals = false
  MapMode = 5
  Placement = pos=(0,0,-170) rot=(0,0,1;0rad)
  _ExternalGeoVersion = 0
  expr: Constraints[31] = Spreadsheet.B14 - Spreadsheet.E2
  expr: Constraints[32] = Spreadsheet.B14 - Spreadsheet.E2
  expr: Constraints[43] = Spreadsheet.E2
  expr: Constraints[46] = Spreadsheet.H7 / 2 + Spreadsheet.H6
  sketch-geometry (18):
    g0: LineSegment StartX=-93.8844 StartY=200 StartZ=0 EndX=-78.8844 EndY=200 EndZ=0
    g1: LineSegment StartX=-200 StartY=72.9731 StartZ=0 EndX=-200 EndY=57.9731 EndZ=0
    g2: LineSegment StartX=-154.307 StartY=57.9731 StartZ=0 EndX=-78.8844 EndY=144.737 EndZ=0
    g3: LineSegment StartX=-159.818 StartY=72.9731 StartZ=0 EndX=-93.8844 EndY=148.821 EndZ=0
    g4: LineSegment StartX=-93.8844 StartY=148.821 StartZ=0 EndX=-93.8844 EndY=200 EndZ=0
    g5: LineSegment StartX=-78.8844 StartY=200 StartZ=0 EndX=-78.8844 EndY=144.737 EndZ=0
    g6: LineSegment StartX=-159.818 StartY=72.9731 StartZ=0 EndX=-200 EndY=72.9731 EndZ=0
    g7: LineSegment StartX=-200 StartY=57.9731 StartZ=0 EndX=-154.307 EndY=57.9731 EndZ=0
    g8: Circle CenterX=-185 CenterY=65.4731 CenterZ=0 NormalX=0 NormalY=0 NormalZ=1 AngleXU=0 Radius=2.2
    g9: Circle CenterX=-86.3844 CenterY=185 CenterZ=0 NormalX=0 NormalY=0 NormalZ=1 AngleXU=0 Radius=2.2
    g10: LineSegment [constr] StartX=-86.3844 StartY=185 StartZ=0 EndX=-93.8844 EndY=185 EndZ=0
    g11: LineSegment [constr] StartX=-86.3844 StartY=185 StartZ=0 EndX=-78.8844 EndY=185 EndZ=0
    g12: LineSegment [constr] StartX=-185 StartY=65.4731 StartZ=0 EndX=-185 EndY=72.9731 EndZ=0
    g13: LineSegment [constr] StartX=-185 StartY=65.4731 StartZ=0 EndX=-185 EndY=57.9731 EndZ=0
    g14: LineSegment [constr] StartX=0 StartY=0 StartZ=0 EndX=-116.596 EndY=101.355 EndZ=0
    g15: LineSegment [constr] StartX=-200 StartY=65.4731 StartZ=0 EndX=-185 EndY=65.4731 EndZ=0
    g16: LineSegment [constr] StartX=-86.3844 StartY=185 StartZ=0 EndX=-86.3844 EndY=200 EndZ=0
    g17: LineSegment [constr] StartX=-126.851 StartY=110.897 StartZ=0 EndX=-123.833 EndY=108.273 EndZ=0
  constraints (51):
    c: Horizontal(g0)
    c: Vertical(g1)
    c: Coincident(g4,g3)
    c: Coincident(g4,g0)
    c: Coincident(g5,g0)
    c: Coincident(g5,g2)
    c: Coincident(g6,g3)
    c: Coincident(g6,g1)
    c: Coincident(g7,g1)
    c: Coincident(g7,g2)
    c: Vertical(g4)
    c: Vertical(g5)
    c: Horizontal(g6)
    c: Horizontal(g7)
    c: Equal(g0,g1)
    c: Coincident(g10,g9)
    c: PointOnObject(g10,g4)
    c: Coincident(g11,g9)
    c: PointOnObject(g11,g5)
    c: Equal(g10,g11)
    c: Perpendicular(g10,g4)
    c: Perpendicular(g5,g11)
    c: Coincident(g12,g8)
    c: PointOnObject(g12,g6)
    c: Coincident(g13,g8)
    c: PointOnObject(g13,g7)
    c: Equal(g12,g13)
    c: Perpendicular(g6,g12)
    c: Perpendicular(g7,g13)
    c: Equal(g8,g9)
    c: Diameter(g8) = 4.4
    c: Distance(g8,g-2) = 185
    c: Distance(g9,g-1) = 185
    c: Coincident(g14,g-1)
    c: Symmetric(g2,g2,g14)
    c: Parallel(g3,g2)
    c: Perpendicular(g14,g2)
    c: DistanceX(g0,g0) = 15
    c: Symmetric(g1,g1,g15)
    c: Coincident(g15,g8)
    c: Coincident(g16,g9)
    c: Symmetric(g0,g0,g16)
    c: Equal(g16,g15)
    c: DistanceY(g16,g16) = 15
    c: Angle(g14,g-1) = 0.715585
    c: Distance(g2,g3) = 14
    c: Distance(g3,g3) = 100.5
    c: Symmetric(g3,g3,g17)
    c: PointOnObject(g17,g-3)
    c: Perpendicular(g17,g3)
    c: Distance(g17,g17) = 4
FEATURE [PartDesign::Pad] Pad008
  Direction = (0,0,1)
  Length = 3
  Length2 = 10
  Placement = pos=(0,0,-170) rot=(0,0,1;0rad)
  Profile = -> Sketch014
  ReferenceAxis = -> Sketch014 [N_Axis]
  Refine = true
  SideType = 0
  Suppressed = false
  Type = 0
  Type2 = 0
FEATURE [PartDesign::Plane] DatumPlane002
  AttachmentSupport = -> [Pad008]
  Length = 367.181
  MapMode = 7
  Placement = pos=(-159.818,72.9731,-167) rot=(0.884029,-0.330525,-0.330525;1.69375rad)
  ResizeMode = 0
  Width = 244.758
FEATURE [Sketcher::SketchObject] Sketch015  label="Sketch018"
  ArcFitTolerance = 1e-06
  AttachmentSupport = -> [DatumPlane002]
  ExternalTypes = [0]
  FullyConstrained = true
  MakeInternals = false
  MapMode = 5
  Placement = pos=(-159.818,72.9731,-167) rot=(0.884029,-0.330525,-0.330525;1.69375rad)
  _ExternalGeoVersion = 0
  sketch-geometry (1):
    g0: LineSegment StartX=0 StartY=0 StartZ=0 EndX=-70.3785 EndY=165.801 EndZ=0
  constraints (3):
    c: Coincident(g0,g-1)
    c: Angle(g0,g-1) = 1.16937
    c: Distance(g0,g0) = 180.12
FEATURE [PartDesign::Plane] DatumPlane003
  AttachmentSupport = -> [Sketch015]
  Length = 385.814
  MapMode = 7
  Placement = pos=(-159.818,72.9731,-167) rot=(0.90674,0.413225,0.084072;2.77674rad)
  ResizeMode = 0
  Width = 436.773
FEATURE [Sketcher::SketchObject] Sketch016  label="Sketch019"
  ArcFitTolerance = 1e-06
  AttachmentSupport = -> [DatumPlane003]
  ExternalTypes = [0]
  FullyConstrained = true
  MakeInternals = false
  MapMode = 5
  Placement = pos=(-159.818,72.9731,-167) rot=(0.90674,0.413225,0.084072;2.77674rad)
  _ExternalGeoVersion = 0
  expr: Constraints[17] = Spreadsheet.N1
  expr: Constraints[24] = Spreadsheet.N1
  expr: Constraints[26] = Spreadsheet.N2
  expr: Constraints[7] = Spreadsheet.H1 + Spreadsheet.H6
  sketch-geometry (10):
    g0: LineSegment StartX=0 StartY=3 StartZ=0 EndX=0 EndY=9.85 EndZ=0
    g1: LineSegment StartX=-3 StartY=0 StartZ=0 EndX=-3 EndY=12.85 EndZ=0
    g2: LineSegment StartX=0 StartY=9.85 StartZ=0 EndX=8 EndY=9.85 EndZ=0
    g3: LineSegment StartX=8 StartY=3 StartZ=0 EndX=0 EndY=3 EndZ=0
    g4: LineSegment StartX=-3 StartY=12.85 StartZ=0 EndX=0 EndY=12.85 EndZ=0
    g5: LineSegment StartX=0 StartY=12.85 StartZ=0 EndX=8 EndY=9.85 EndZ=0
    g6: LineSegment StartX=8 StartY=3 StartZ=0 EndX=9e-16 EndY=0 EndZ=0
    g7: LineSegment StartX=0 StartY=0 StartZ=0 EndX=-3 EndY=0 EndZ=0
    g8: LineSegment [constr] StartX=0 StartY=12.85 StartZ=0 EndX=0 EndY=9.85 EndZ=0
    g9: LineSegment [constr] StartX=0 StartY=3 StartZ=0 EndX=0 EndY=0 EndZ=0
  constraints (28):
    c: PointOnObject(g0,g-2)
    c: PointOnObject(g0,g-2)
    c: Vertical(g1)
    c: Coincident(g2,g0)
    c: Horizontal(g2)
    c: Coincident(g3,g0)
    c: Horizontal(g3)
    c: DistanceY(g0,g0) = 6.85
    c: Coincident(g4,g1)
    c: Horizontal(g4)
    c: Coincident(g5,g4)
    c: Coincident(g5,g2)
    c: Coincident(g6,g3)
    c: Coincident(g6,g-1)
    c: Coincident(g7,g6)
    c: Coincident(g7,g1)
    c: Horizontal(g7)
    c: DistanceY(g0,g4) = 3
    c: PointOnObject(g4,g-2)
    c: Coincident(g8,g4)
    c: Coincident(g8,g0)
    c: Coincident(g9,g0)
    c: Coincident(g9,g6)
    c: Equal(g8,g9)
    c: DistanceX(g4,g4) = 3
    c: Equal(g2,g3)
    c: DistanceX(g3,g3) = 8
    c: DistanceY(g1,g1) = 12.85
FEATURE [PartDesign::Plane] DatumPlane004
  AttachmentSupport = -> [Sketch016]
  Length = 379.502
  MapMode = 7
  Placement = pos=(-157.734,71.1614,-165.828) rot=(-0.355237,0.779497,0.515938;3.60346rad)
  ResizeMode = 0
  Width = 365.605
FEATURE [Sketcher::SketchObject] Sketch017  label="Sketch020"
  ArcFitTolerance = 1e-06
  AttachmentSupport = -> [DatumPlane004]
  ExternalTypes = [0]
  FullyConstrained = true
  MakeInternals = false
  MapMode = 5
  Placement = pos=(-157.734,71.1614,-165.828) rot=(-0.355237,0.779497,0.515938;3.60346rad)
  _ExternalGeoVersion = 0
  expr: Constraints[18] = Spreadsheet.H7 / 2 + Spreadsheet.H6
  expr: Constraints[21] = (Spreadsheet.O1 + Spreadsheet.N1) * tan(90 - 67) * 0.95
  expr: Constraints[22] = Spreadsheet.N3
  sketch-geometry (8):
    g0: LineSegment [constr] StartX=50.25 StartY=87.0356 StartZ=0 EndX=0 EndY=174.071 EndZ=0
    g1: LineSegment [constr] StartX=0 StartY=174.071 StartZ=0 EndX=-100.5 EndY=174.071 EndZ=0
    g2: LineSegment [constr] StartX=-100.5 StartY=174.071 StartZ=0 EndX=-150.75 EndY=87.0356 EndZ=0
    g3: LineSegment [constr] StartX=-150.75 StartY=87.0356 StartZ=0 EndX=-100.5 EndY=-1.42e-14 EndZ=0
    g4: LineSegment [constr] StartX=-100.5 StartY=-1.42e-14 StartZ=0 EndX=0 EndY=0 EndZ=0
    g5: LineSegment [constr] StartX=0 StartY=0 StartZ=0 EndX=50.25 EndY=87.0356 EndZ=0
    g6: Circle [constr] CenterX=-50.25 CenterY=87.0356 CenterZ=0 NormalX=0 NormalY=0 NormalZ=1 AngleXU=0 Radius=100.5
    g7: LineSegment StartX=25 StartY=43.3013 StartZ=0 EndX=-3.19576 EndY=-5.53523 EndZ=0
  constraints (20):
    c: Coincident(g0,g1)
    c: Coincident(g1,g2)
    c: Coincident(g2,g3)
    c: Coincident(g3,g4)
    c: Coincident(g4,g5)
    c: Coincident(g5,g0)
    c: Equal(g0, g1-g5) x5
    c: PointOnObject(g0,g6)
    c: PointOnObject(g1,g6)
    c: PointOnObject(g2,g6)
    c: PointOnObject(g3,g6)
    c: PointOnObject(g5,g6)
    c: Coincident(g4,g-1)
    c: Horizontal(g1)
    c: DistanceX(g1,g1) = 100.5
    c: PointOnObject(g7,g5)
    c: PointOnObject(g4,g7)
    c: Distance(g7,g-1) = 6.39153
    c: Distance(g7,g-1) = 50
    c: PointOnObject(g4,g6)
FEATURE [PartDesign::AdditivePipe] AdditivePipe001
  AuxiliaryCurvilinear = true
  AuxiliarySpineTangent = false
  BaseFeature = -> Pad008
  Binormal = (0,0,0)
  Mode = 0
  Placement = pos=(0,0,-170) rot=(0,0,1;0rad)
  Profile = -> Sketch016
  Refine = true
  Spine = -> Sketch017
  SpineTangent = false
  Suppressed = false
  Transformation = 0
  Transition = 0
FEATURE [PartDesign::Plane] DatumPlane005
  AttachmentSupport = -> [AdditivePipe001]
  Length = 367.181
  MapMode = 45
  Placement = pos=(-126.851,110.897,-167) rot=(0.255595,0.68362,0.68362;2.64112rad)
  ResizeMode = 0
  Width = 244.758
FEATURE [PartDesign::Mirrored] Mirrored
  BaseFeature = -> AdditivePipe001
  MirrorPlane = -> DatumPlane005
  Originals = -> [AdditivePipe001]
  Placement = pos=(0,0,-170) rot=(0,0,1;0rad)
  Refine = true
  Suppressed = false
  TransformMode = 0
FEATURE [App::Link] Link050  label="Mirror rails001"
  LinkedObject = -> Part011
FEATURE [PartDesign::Plane] DatumPlane006
  Length = 435.009
  MapMode = 1
  Placement = pos=(-157.73,71.16,-165.83) rot=(-0.36,0.78,0.52;3.60341rad)
  ResizeMode = 0
  Width = 386.48
FEATURE [Sketcher::SketchObject] Sketch018  label="Sketch021"
  ArcFitTolerance = 1e-06
  AttachmentSupport = -> [DatumPlane006]
  ExternalTypes = [0]
  FullyConstrained = true
  MakeInternals = false
  MapMode = 5
  Placement = pos=(-157.73,71.16,-165.83) rot=(-0.358497,0.776744,0.51783;3.60341rad)
  _ExternalGeoVersion = 0
  expr: Constraints[22] = Spreadsheet.H7
  expr: Constraints[2] = Spreadsheet.H6
  sketch-geometry (8):
    g0: LineSegment [constr] StartX=0 StartY=0 StartZ=0 EndX=-0.5 EndY=0 EndZ=0
    g1: LineSegment StartX=-0.5 StartY=0 StartZ=0 EndX=49.5 EndY=86.6025 EndZ=0
    g2: LineSegment StartX=49.5 StartY=86.6025 StartZ=0 EndX=-0.5 EndY=173.205 EndZ=0
    g3: LineSegment StartX=-0.5 StartY=173.205 StartZ=0 EndX=-100.5 EndY=173.205 EndZ=0
    g4: LineSegment StartX=-100.5 StartY=173.205 StartZ=0 EndX=-150.5 EndY=86.6025 EndZ=0
    g5: LineSegment StartX=-150.5 StartY=86.6025 StartZ=0 EndX=-100.5 EndY=0 EndZ=0
    g6: LineSegment StartX=-100.5 StartY=0 StartZ=0 EndX=-0.5 EndY=0 EndZ=0
    g7: Circle [constr] CenterX=-50.5 CenterY=86.6025 CenterZ=0 NormalX=0 NormalY=0 NormalZ=1 AngleXU=0 Radius=100
  constraints (19):
    c: Coincident(g0,g-1)
    c: Horizontal(g0)
    c: DistanceX(g0,g0) = 0.5
    c: Coincident(g1,g2)
    c: Coincident(g2,g3)
    c: Coincident(g3,g4)
    c: Coincident(g4,g5)
    c: Coincident(g5,g6)
    c: Coincident(g6,g1)
    c: Equal(g1, g2-g6) x5
    c: PointOnObject(g1,g7)
    c: PointOnObject(g2,g7)
    c: PointOnObject(g3,g7)
    c: PointOnObject(g4,g7)
    c: PointOnObject(g5,g7)
    c: PointOnObject(g6,g7)
    c: Horizontal(g6)
    c: Coincident(g1,g0)
    c: Diameter(g7) = 200
FEATURE [PartDesign::Pad] Pad009
  Direction = (-0.697931,0.602571,-0.38704)
  Length = 6.35
  Length2 = 10
  Placement = pos=(-157.73,71.16,-165.83) rot=(-0.36,0.78,0.52;3.60341rad)
  Profile = -> Sketch018
  ReferenceAxis = -> Sketch018 [N_Axis]
  Refine = true
  Reversed = true
  SideType = 0
  Suppressed = false
  Type = 0
  Type2 = 0
  expr: Length = Spreadsheet.H1
FEATURE [App::Link] Link051  label="Mirror rails002"
  LinkPlacement = pos=(0,0,0) rot=(0,0,1;-1.5708rad)
  LinkedObject = -> Part011
  Placement = pos=(0,0,0) rot=(0,0,1;-1.5708rad)
FEATURE [PartDesign::Fillet] Fillet007
  Base = -> Pad009 [Edge1,Edge14,Edge2,Edge5,Edge8,Edge11]
  BaseFeature = -> Pad009
  Placement = pos=(-157.73,71.16,-165.83) rot=(-0.36,0.78,0.52;3.60341rad)
  Radius = 1
  Refine = true
  SupportTransform = false
  Suppressed = false
  UseAllEdges = false
FEATURE [PartDesign::Body] Body006
  AllowCompound = false
  Group = -> [DatumPlane006,Sketch018,Pad009,Fillet007]
  Origin = -> Origin018
  Tip = -> Fillet007
FEATURE [PartDesign::Pocket] Pocket003
  BaseFeature = -> Mirrored
  Direction = (0,0,-1)
  Length = 5
  Length2 = 5
  Placement = pos=(0,0,-170) rot=(0,0,1;0rad)
  Profile = -> Sketch014
  ReferenceAxis = -> Sketch014 [N_Axis]
  Refine = true
  SideType = 0
  Suppressed = false
  Type = 0
  Type2 = 0
FEATURE [PartDesign::Fillet] Fillet008
  Base = -> Pocket003 [Edge8,Edge36,Edge5,Edge34,Edge76,Edge47,Edge72,Edge40,Edge38,Edge50,Edge74,Edge52,Edge51,Edge49,Edge53,Edge75,Edge77,Edge78,Edge65,Edge73,Edge69,Edge67,Edge71,Edge55,Edge57,Edge59,Edge61,Edge62]
  BaseFeature = -> Pocket003
  Placement = pos=(0,0,-170) rot=(0,0,1;0rad)
  Radius = 1
  Refine = true
  SupportTransform = false
  Suppressed = false
  UseAllEdges = false
FEATURE [PartDesign::Body] Body005
  AllowCompound = true
  Group = -> [Binder002,DatumPlane001,Sketch014,Pad008,DatumPlane002,Sketch015,DatumPlane003,Sketch016,DatumPlane004,Sketch017,AdditivePipe001,DatumPlane005,Mirrored,Pocket003,Fillet008]
  Origin = -> Origin017
  Tip = -> Fillet008
FEATURE [App::Part] Part011  label="Mirror rails"
  Group = -> [Body005,Body006]
  Origin = -> Origin016
FEATURE [Part::Feature] Part__Feature003  label="GT2 20T 8mm - Deflanged"
  Placement = pos=(-1.776e-13,-0.0153703,26.25) rot=(-0.357407,0.862856,0.357407;1.71777rad)
  shape: bbox 4.805 x 4.803 x 3.001 mm, 10 faces (baked)
FEATURE [Part::Feature] Part__Feature004  label="GT2 20T 8mm - Deflanged001"
  Placement = pos=(-1.776e-13,-0.0153703,26.25) rot=(-0.357407,0.862856,0.357407;1.71777rad)
  shape: bbox 4.803 x 4.805 x 3.001 mm, 10 faces (baked)
FEATURE [Part::Feature] Part__Feature005  label="GT2 20T 8mm - Deflanged002"
  Placement = pos=(-1.776e-13,-0.0153703,26.25) rot=(-0.357407,0.862856,0.357407;1.71777rad)
  shape: bbox 16 x 16 x 16 mm, 93 faces (baked)
FEATURE [App::Part] GT2_20T_8mm___Deflanged  label="GT2 20T 8mm - Deflanged003"
  Group = -> [Part__Feature003,Part__Feature004,Part__Feature005]
  Origin = -> Origin019
FEATURE [Part::Feature] Part__Feature006  label="Cube Insert"
  shape: bbox 17.1 x 17.1 x 18.4 mm, 349 faces (baked)
FEATURE [Part::Feature] Part__Feature007  label="Maxwell 8mm x 50 Rod"
  Placement = pos=(208,-26.5,89.8988) rot=(-1,0,0;1.5708rad)
  shape: bbox 8 x 8 x 100 mm, 5 faces (baked)
FEATURE [Part::Feature] Part__Feature008  label="5mm x 8mm Coupler"
  Placement = pos=(208,-26.5,41.2976) rot=(0,0,1;0rad)
  shape: bbox 19.99 x 20.01 x 25.01 mm, 24 faces (baked)
FEATURE [App::Part] __8mm_coupler  label="5-8mm coupler"
  Group = -> [Part__Feature007,Part__Feature008]
  Origin = -> Origin020
  Placement = pos=(-208,-26.5,159.849) rot=(1,0,0;3.14159rad)
FEATURE [App::Part] Qter_bot_gripper_Shaft_v4  label="Qter bot gripper Shaft v4"
  Group = -> [GT2_20T_8mm___Deflanged,Part__Feature006,__8mm_coupler]
  Origin = -> Origin021
  Placement = pos=(0,0,-17.69) rot=(0,1,0;3.14159rad)
  expr: .Placement.Base.z = -Spreadsheet.B2 / 2 + 10.25 mm
FEATURE [Part::Feature] Part__Feature009  label="GT2 20T 8mm - Deflanged004"
  Placement = pos=(-1.776e-13,-0.0153703,26.25) rot=(-0.357407,0.862856,0.357407;1.71777rad)
  shape: bbox 4.805 x 4.803 x 3.001 mm, 10 faces (baked)
FEATURE [Part::Feature] Part__Feature010  label="GT2 20T 8mm - Deflanged005"
  Placement = pos=(-1.776e-13,-0.0153703,26.25) rot=(-0.357407,0.862856,0.357407;1.71777rad)
  shape: bbox 4.803 x 4.805 x 3.001 mm, 10 faces (baked)
FEATURE [Part::Feature] Part__Feature011  label="GT2 20T 8mm - Deflanged006"
  Placement = pos=(-1.776e-13,-0.0153703,26.25) rot=(-0.357407,0.862856,0.357407;1.71777rad)
  shape: bbox 16 x 16 x 16 mm, 93 faces (baked)
FEATURE [App::Part] GT2_20T_8mm___Deflanged001  label="GT2 20T 8mm - Deflanged007"
  Group = -> [Part__Feature009,Part__Feature010,Part__Feature011]
  Origin = -> Origin022
FEATURE [Part::Feature] Part__Feature012  label="Cube Insert001"
  shape: bbox 17.1 x 17.1 x 18.4 mm, 349 faces (baked)
FEATURE [Part::Feature] Part__Feature013  label="Maxwell 8mm x 50 Rod001"
  Placement = pos=(208,-26.5,89.8988) rot=(-1,0,0;1.5708rad)
  shape: bbox 8 x 8 x 100 mm, 5 faces (baked)
FEATURE [Part::Feature] Part__Feature014  label="5mm x 8mm Coupler001"
  Placement = pos=(208,-26.5,41.2976) rot=(0,0,1;0rad)
  shape: bbox 19.99 x 20.01 x 25.01 mm, 24 faces (baked)
FEATURE [App::Part] __8mm_coupler001  label="5-8mm coupler001"
  Group = -> [Part__Feature013,Part__Feature014]
  Origin = -> Origin023
  Placement = pos=(-208,-26.5,148.849) rot=(1,0,0;3.14159rad)
FEATURE [App::Part] Qter_bot_gripper_Shaft_v005  label="Qter bot gripper Shaft v005"
  Group = -> [GT2_20T_8mm___Deflanged001,Part__Feature012,__8mm_coupler001]
  Origin = -> Origin024
  Placement = pos=(0,0,-18.99) rot=(0,1,0;3.14159rad)
  expr: .Placement.Base.z = -Spreadsheet.B2 / 2 + 8.95 mm
FEATURE [App::Part] Part008  label="Gripper"
  Group = -> [cube_gripper_2,cube_gripper_stl,cube_gripper_3,Qter_bot_gripper_Shaft_v4,Qter_bot_gripper_Shaft_v005]
  Origin = -> Origin009
FEATURE [Sketcher::SketchObject] Sketch019  label="Sketch022"
  ArcFitTolerance = 1e-06
  AttachmentSupport = -> [YZ_Plane026]
  ExternalTypes = [0]
  FullyConstrained = true
  MakeInternals = false
  MapMode = 5
  Placement = pos=(0,0,0) rot=(0.57735,0.57735,0.57735;2.0944rad)
  _ExternalGeoVersion = 0
  expr: Constraints[4] = Spreadsheet.N16
  sketch-geometry (15):
    g0: LineSegment StartX=-49.5728 StartY=0 StartZ=0 EndX=-49.5728 EndY=-3 EndZ=0
    g1: LineSegment [constr] StartX=-49.5728 StartY=-3 StartZ=0 EndX=-4.57276 EndY=-3 EndZ=0
    g2: LineSegment [constr] StartX=-4.57276 StartY=-3 StartZ=0 EndX=-38.5347 EndY=-32.5227 EndZ=0
    g3: LineSegment StartX=-38.5347 StartY=-32.5227 StartZ=0 EndX=-36.5665 EndY=-34.7868 EndZ=0
    g4: LineSegment StartX=-36.5665 StartY=-34.7868 StartZ=0 EndX=0 EndY=-3 EndZ=0
    g5: LineSegment StartX=15 StartY=0 StartZ=0 EndX=-49.5728 EndY=0 EndZ=0
    g6: LineSegment StartX=0 StartY=-3 StartZ=0 EndX=15 EndY=-3 EndZ=0
    g7: LineSegment StartX=15 StartY=0 StartZ=0 EndX=15 EndY=-3 EndZ=0
    g8: LineSegment [constr] StartX=-4.57276 StartY=-3 StartZ=0 EndX=0 EndY=-3 EndZ=0
    g9: LineSegment StartX=-49.5728 StartY=-3 StartZ=0 EndX=-34.5728 EndY=-3 EndZ=0
    g10: LineSegment StartX=-38.5347 StartY=-32.5227 StartZ=0 EndX=-27.214 EndY=-22.6818 EndZ=0
    g11: LineSegment StartX=-4.57276 StartY=-3 StartZ=0 EndX=-24.9499 EndY=-20.7136 EndZ=0
    g12: LineSegment StartX=-31.5728 StartY=-3 StartZ=0 EndX=-4.57276 EndY=-3 EndZ=0
    g13: ArcOfCircle CenterX=-4.57276 CenterY=-3 CenterZ=0 NormalX=0 NormalY=0 NormalZ=1 AngleXU=0 Radius=27 StartAngle=3.14159 EndAngle=3.85718
    g14: ArcOfCircle CenterX=-4.57276 CenterY=-3 CenterZ=0 NormalX=0 NormalY=0 NormalZ=1 AngleXU=0 Radius=30 StartAngle=3.14159 EndAngle=3.85718
  constraints (42):
    c: PointOnObject(g0,g-1)
    c: Vertical(g0)
    c: Horizontal(g1)
    c: Coincident(g3,g2)
    c: Angle(g1,g2) = 0.715585
    c: Coincident(g2,g1)
    c: Coincident(g1,g0)
    c: Parallel(g2,g4)
    c: Coincident(g4,g3)
    c: Perpendicular(g3,g2)
    c: Equal(g0,g3)
    c: DistanceY(g0,g0) = 3
    c: Coincident(g5,g0)
    c: PointOnObject(g4,g-2)
    c: Coincident(g6,g4)
    c: Horizontal(g6)
    c: PointOnObject(g5,g-1)
    c: Coincident(g7,g5)
    c: Coincident(g7,g6)
    c: Vertical(g7)
    c: Coincident(g8,g1)
    c: Coincident(g8,g4)
    c: Horizontal(g8)
    c: DistanceX(g6,g6) = 15
    c: DistanceX(g1,g1) = 45
    c: Equal(g1,g2)
    c: Coincident(g9,g0)
    c: PointOnObject(g9,g1)
    c: Coincident(g10,g2)
    c: PointOnObject(g10,g2)
    c: Coincident(g11,g1)
    c: PointOnObject(g11,g2)
    c: PointOnObject(g12,g1)
    c: Coincident(g12,g1)
    c: Coincident(g13,g1)
    c: Coincident(g13,g12)
    c: Coincident(g13,g11)
    c: Coincident(g14,g1)
    c: Coincident(g14,g9)
    c: Coincident(g14,g10)
    c: DistanceX(g9,g12) = 3
    c: DistanceX(g9,g9) = 15
FEATURE [PartDesign::Pad] Pad010
  Direction = (1,0,0)
  Length = 15
  Length2 = 15
  Placement = pos=(0,0,0) rot=(1,1,1;2.0944rad)
  Profile = -> Sketch019
  ReferenceAxis = -> Sketch019 [N_Axis]
  Refine = true
  Reversed = true
  SideType = 1
  Suppressed = false
  Type = 0
  Type2 = 0
  expr: Length = Spreadsheet.E2
  expr: Length2 = Spreadsheet.E2
FEATURE [App::Link] Link052  label="Mirror rails 003"
  LinkPlacement = pos=(-45,65,170) rot=(0,0,1;3.14159rad)
  LinkedObject = -> Part012
  Placement = pos=(-45,65,170) rot=(0,0,1;3.14159rad)
  expr: .Placement.Base.x = -Spreadsheet.B5
  expr: .Placement.Base.z = Spreadsheet.B1 - Spreadsheet.E1
FEATURE [Sketcher::SketchObject] Sketch020  label="Sketch023"
  ArcFitTolerance = 1e-06
  AttachmentSupport = -> [XY_Plane026]
  ExternalGeometry = -> [Pad010]
  ExternalTypes = [0]
  FullyConstrained = true
  MakeInternals = false
  MapMode = 5
  _ExternalGeoVersion = 0
  sketch-geometry (4):
    g0: Circle CenterX=0 CenterY=9.8 CenterZ=0 NormalX=0 NormalY=0 NormalZ=1 AngleXU=0 Radius=2.2
    g1: Circle CenterX=0 CenterY=-44.3728 CenterZ=0 NormalX=0 NormalY=0 NormalZ=1 AngleXU=0 Radius=2.2
    g2: LineSegment [constr] StartX=-4e-16 StartY=12 StartZ=0 EndX=-4e-16 EndY=15 EndZ=0
    g3: LineSegment [constr] StartX=0 StartY=-46.5728 StartZ=0 EndX=0 EndY=-49.5728 EndZ=0
  constraints (13):
    c: PointOnObject(g0,g-2)
    c: PointOnObject(g1,g-2)
    c: Diameter(g0) = 4.4
    c: PointOnObject(g2,g0)
    c: Symmetric(g-3,g-3,g2)
    c: Vertical(g2)
    c: PointOnObject(g3,g1)
    c: Vertical(g3)
    c: Equal(g3,g2)
    c: DistanceY(g2,g2) = 3
    c: Equal(g0,g1)
    c: PointOnObject(g3,g-4)
    c: PointOnObject(g3,g-2)
FEATURE [PartDesign::Pocket] Pocket004
  BaseFeature = -> Pad010
  Direction = (0,0,-1)
  Length = 5
  Length2 = 5
  Placement = pos=(0,0,0) rot=(1,1,1;2.0944rad)
  Profile = -> Sketch020
  ReferenceAxis = -> Sketch020 [N_Axis]
  Refine = true
  SideType = 0
  Suppressed = false
  Type = 0
  Type2 = 0
FEATURE [PartDesign::Fillet] Fillet009
  Base = -> Pocket004 [Edge4,Edge30,Edge36,Edge37,Edge38,Edge39,Edge42,Edge40,Edge41,Edge1,Edge7,Edge35]
  BaseFeature = -> Pocket004
  Placement = pos=(0,0,0) rot=(1,1,1;2.0944rad)
  Radius = 1
  Refine = true
  SupportTransform = false
  Suppressed = false
  UseAllEdges = false
FEATURE [PartDesign::Body] Body007
  AllowCompound = true
  Group = -> [Sketch019,Pad010,Sketch020,Pocket004,Fillet009]
  Origin = -> Origin026
  Tip = -> Fillet009
FEATURE [PartDesign::Plane] DatumPlane007
  Length = 123.697
  MapMode = 1
  Placement = pos=(0,0,-3) rot=(1,0,0;0.715585rad)
  ResizeMode = 0
  Width = 164.078
  expr: .Placement.Rotation.Angle = Spreadsheet.N16
FEATURE [Sketcher::SketchObject] Sketch021  label="Sketch024"
  ArcFitTolerance = 1e-06
  AttachmentSupport = -> [DatumPlane007]
  ExternalTypes = [0]
  FullyConstrained = true
  MakeInternals = false
  MapMode = 5
  Placement = pos=(0,-2e-16,-3) rot=(1,0,0;0.715585rad)
  _ExternalGeoVersion = 0
  expr: Constraints[10] = Spreadsheet.N15
  sketch-geometry (4):
    g0: LineSegment StartX=-50 StartY=0 StartZ=0 EndX=-50 EndY=-100 EndZ=0
    g1: LineSegment StartX=-50 StartY=-100 StartZ=0 EndX=50 EndY=-100 EndZ=0
    g2: LineSegment StartX=50 StartY=-100 StartZ=0 EndX=50 EndY=0 EndZ=0
    g3: LineSegment StartX=50 StartY=0 StartZ=0 EndX=-50 EndY=0 EndZ=0
  constraints (11):
    c: Coincident(g0,g1)
    c: Coincident(g1,g2)
    c: Coincident(g2,g3)
    c: Coincident(g3,g0)
    c: Vertical(g0)
    c: Vertical(g2)
    c: Horizontal(g1)
    c: PointOnObject(g0,g-1)
    c: Equal(g3,g0)
    c: Symmetric(g0,g2,g-2)
    c: DistanceY(g0,g0) = 100
FEATURE [PartDesign::Pad] Pad011
  Direction = (0,-0.656059,0.75471)
  Length = 6.35
  Length2 = 10
  Placement = pos=(0,0,-3) rot=(1,0,0;0.715585rad)
  Profile = -> Sketch021
  ReferenceAxis = -> Sketch021 [N_Axis]
  Refine = true
  Reversed = true
  SideType = 0
  Suppressed = false
  Type = 0
  Type2 = 0
  expr: Length = Spreadsheet.H1
FEATURE [PartDesign::Body] Body008
  AllowCompound = false
  Group = -> [DatumPlane007,Sketch021,Pad011]
  Origin = -> Origin027
  Tip = -> Pad011
FEATURE [App::Part] Part012  label="Mirror rails 2"
  Group = -> [Body007,Body008]
  Origin = -> Origin025
FEATURE [PartDesign::Plane] DatumPlane008
  Length = 122.812
  MapMode = 1
  Placement = pos=(0,0,0) rot=(-0.052562,0.997379,0.049714;1.78261rad)
  ResizeMode = 0
  Width = 80.6103
FEATURE [Sketcher::SketchObject] Sketch022  label="Sketch025"
  ArcFitTolerance = 1e-06
  AttachmentSupport = -> [DatumPlane008]
  ExternalTypes = [0]
  FullyConstrained = true
  MakeInternals = false
  MapMode = 5
  Placement = pos=(0,0,0) rot=(-0.052562,0.997379,0.049714;1.78261rad)
  _ExternalGeoVersion = 0
  sketch-geometry (4):
    g0: LineSegment StartX=0 StartY=3 StartZ=0 EndX=60 EndY=3 EndZ=0
    g1: LineSegment StartX=60 StartY=3 StartZ=0 EndX=60 EndY=-30 EndZ=0
    g2: LineSegment StartX=60 StartY=-30 StartZ=0 EndX=0 EndY=-30 EndZ=0
    g3: LineSegment StartX=0 StartY=-30 StartZ=0 EndX=0 EndY=3 EndZ=0
  constraints (12):
    c: Horizontal(g0)
    c: Horizontal(g2)
    c: Vertical(g1)
    c: Vertical(g3)
    c: DistanceX(g2,g2) = 60
    c: Coincident(g0,g3)
    c: Coincident(g3,g2)
    c: Coincident(g2,g1)
    c: Coincident(g1,g0)
    c: DistanceY(g1,g-1) = 30
    c: PointOnObject(g2,g-2)
    c: DistanceY(g-1,g0) = 3
FEATURE [PartDesign::Pad] Pad012
  Direction = (0.971927,0.111395,-0.207242)
  Length = 3
  Length2 = 10
  Placement = pos=(0,0,0) rot=(-0.052562,0.997379,0.049714;1.78261rad)
  Profile = -> Sketch022
  ReferenceAxis = -> Sketch022 [N_Axis]
  Refine = true
  SideType = 0
  Suppressed = false
  Type = 0
  Type2 = 0
FEATURE [Sketcher::SketchObject] Sketch023  label="Sketch026"
  ArcFitTolerance = 1e-06
  AttachmentSupport = -> [XZ_Plane029]
  ExternalGeometry = -> [Pad012]
  ExternalTypes = [0]
  FullyConstrained = true
  MakeInternals = false
  MapMode = 5
  Placement = pos=(0,0,0) rot=(1,0,0;1.5708rad)
  _ExternalGeoVersion = 0
  expr: Constraints[31] = Spreadsheet.E2
  sketch-geometry (10):
    g0: LineSegment StartX=1 StartY=0 StartZ=0 EndX=-9.83372 EndY=-59.291 EndZ=0
    g1: LineSegment StartX=-9.83372 StartY=-59.291 StartZ=0 EndX=31 EndY=-59.291 EndZ=0
    g2: LineSegment StartX=31 StartY=-59.291 StartZ=0 EndX=31 EndY=0 EndZ=0
    g3: LineSegment StartX=31 StartY=0 StartZ=0 EndX=1 EndY=0 EndZ=0
    g4: Circle CenterX=16 CenterY=-11.2 CenterZ=0 NormalX=0 NormalY=0 NormalZ=1 AngleXU=0 Radius=2.2
    g5: Circle CenterX=16 CenterY=-48.091 CenterZ=0 NormalX=0 NormalY=0 NormalZ=1 AngleXU=0 Radius=2.2
    g6: LineSegment [constr] StartX=16 StartY=-9 StartZ=0 EndX=16 EndY=0 EndZ=0
    g7: LineSegment [constr] StartX=18.2 StartY=-11.2 StartZ=0 EndX=31 EndY=-11.2 EndZ=0
    g8: LineSegment [constr] StartX=16 StartY=-50.291 StartZ=0 EndX=16 EndY=-59.291 EndZ=0
    g9: LineSegment [constr] StartX=18.2 StartY=-48.091 StartZ=0 EndX=31 EndY=-48.091 EndZ=0
  constraints (33):
    c: Coincident(g0,g1)
    c: Coincident(g1,g2)
    c: Coincident(g2,g3)
    c: Coincident(g3,g0)
    c: Vertical(g2)
    c: Horizontal(g1)
    c: Horizontal(g3)
    c: Coincident(g0,g-3)
    c: DistanceX(g3,g3) = 30
    c: Diameter(g5) = 4.4
    c: Equal(g4,g5)
    c: PointOnObject(g6,g4)
    c: PointOnObject(g6,g3)
    c: Vertical(g6)
    c: PointOnObject(g7,g4)
    c: PointOnObject(g7,g2)
    c: Horizontal(g7)
    c: PointOnObject(g8,g5)
    c: PointOnObject(g8,g1)
    c: Vertical(g8)
    c: PointOnObject(g9,g5)
    c: PointOnObject(g9,g2)
    c: Horizontal(g9)
    c: Perpendicular(g4,g6)
    c: Perpendicular(g4,g7)
    c: Perpendicular(g5,g8)
    c: Perpendicular(g5,g9)
    c: Equal(g7,g9)
    c: Equal(g8,g6)
    c: DistanceY(g6,g6) = 9
    c: DistanceX(g-1,g0) = 1
    c: Distance(g4,g2) = 15
    c: PointOnObject(g0,g-1)
FEATURE [PartDesign::Pad] Pad013
  BaseFeature = -> Pad012
  Direction = (0,-1,2e-16)
  Length = 3
  Length2 = 10
  Placement = pos=(0,0,0) rot=(-0.052562,0.997379,0.049714;1.78261rad)
  Profile = -> Sketch023
  ReferenceAxis = -> Sketch023 [N_Axis]
  Refine = true
  SideType = 0
  Suppressed = false
  Type = 0
  Type2 = 0
FEATURE [Sketcher::SketchObject] Sketch024  label="Sketch027"
  ArcFitTolerance = 1e-06
  AttachmentSupport = -> [XY_Plane029]
  ExternalGeometry = -> [Pad013]
  ExternalTypes = [0]
  FullyConstrained = true
  MakeInternals = false
  MapMode = 5
  _ExternalGeoVersion = 0
  sketch-geometry (3):
    g0: LineSegment StartX=3.30508 StartY=-29.31 StartZ=0 EndX=31 EndY=-3 EndZ=0
    g1: LineSegment StartX=3.30508 StartY=-29.31 StartZ=0 EndX=0 EndY=0 EndZ=0
    g2: LineSegment StartX=0 StartY=0 StartZ=0 EndX=31 EndY=-3 EndZ=0
  constraints (7):
    c: Coincident(g1,g-1)
    c: Coincident(g2,g1)
    c: Coincident(g2,g0)
    c: Coincident(g0,g-4)
    c: Coincident(g1,g0)
    c: PointOnObject(g0,g-3)
    c: DistanceY(g-3,g0) = 0.5
FEATURE [PartDesign::Pad] Pad014
  BaseFeature = -> Pad013
  Direction = (0,0,1)
  Length = 3
  Length2 = 0
  Placement = pos=(0,0,0) rot=(-0.052562,0.997379,0.049714;1.78261rad)
  Profile = -> Sketch024
  ReferenceAxis = -> Sketch024 [N_Axis]
  Refine = true
  Reversed = true
  SideType = 1
  Suppressed = false
  Type = 0
  Type2 = 0
FEATURE [PartDesign::Plane] DatumPlane009
  AttachmentSupport = -> [Pad014]
  Length = 77.24
  MapMode = 5
  Placement = pos=(-9.71e-14,-4.01e-14,-59.291) rot=(0.666313,0.745672,0;3.14159rad)
  ResizeMode = 0
  Width = 90.6474
FEATURE [Sketcher::SketchObject] Sketch025  label="Sketch028"
  ArcFitTolerance = 1e-06
  AttachmentSupport = -> [DatumPlane009]
  ExternalGeometry = -> [Pad014]
  ExternalTypes = [0]
  FullyConstrained = false
  MakeInternals = false
  MapMode = 5
  Placement = pos=(-9.71e-14,-4.01e-14,-59.291) rot=(0.666313,0.745672,0;3.14159rad)
  _ExternalGeoVersion = 0
  sketch-geometry (4):
    g0: LineSegment StartX=-37.8521 StartY=-23.1435 StartZ=0 EndX=19.9271 EndY=-23.1435 EndZ=0
    g1: LineSegment StartX=19.9271 StartY=-23.1435 StartZ=0 EndX=19.9271 EndY=35.7796 EndZ=0
    g2: LineSegment StartX=19.9271 StartY=35.7796 StartZ=0 EndX=-37.8521 EndY=35.7796 EndZ=0
    g3: LineSegment StartX=-37.8521 StartY=35.7796 StartZ=0 EndX=-37.8521 EndY=-23.1435 EndZ=0
  constraints (8):
    c: Coincident(g0,g1)
    c: Coincident(g1,g2)
    c: Coincident(g2,g3)
    c: Coincident(g3,g0)
    c: Horizontal(g0)
    c: Horizontal(g2)
    c: Vertical(g1)
    c: Vertical(g3)
FEATURE [PartDesign::Pocket] Pocket005
  BaseFeature = -> Pad014
  Direction = (0,0,1)
  Length = 5
  Length2 = 5
  Placement = pos=(0,0,0) rot=(-0.052562,0.997379,0.049714;1.78261rad)
  Profile = -> Sketch025
  ReferenceAxis = -> Sketch025 [N_Axis]
  Refine = true
  Reversed = true
  SideType = 0
  Suppressed = false
  Type = 0
  Type2 = 0
FEATURE [Sketcher::SketchObject] Sketch026  label="Sketch029"
  ArcFitTolerance = 1e-06
  AttachmentSupport = -> [DatumPlane009]
  ExternalGeometry = -> [Pocket005]
  ExternalTypes = [0]
  FullyConstrained = true
  MakeInternals = false
  MapMode = 5
  Placement = pos=(-9.71e-14,-4.01e-14,-59.291) rot=(0.666313,0.745672,0;3.14159rad)
  _ExternalGeoVersion = 0
  sketch-geometry (3):
    g0: LineSegment StartX=-29.49 StartY=-9.43984 StartZ=0 EndX=-6.45476 EndY=30.4686 EndZ=0
    g1: LineSegment StartX=-6.45476 StartY=30.4686 StartZ=0 EndX=-1.94888 EndY=-9.49013 EndZ=0
    g2: LineSegment StartX=-29.49 StartY=-9.43984 StartZ=0 EndX=-1.94888 EndY=-9.49013 EndZ=0
  constraints (6):
    c: Coincident(g0,g-3)
    c: Coincident(g1,g0)
    c: Coincident(g2,g0)
    c: Coincident(g2,g1)
    c: Coincident(g1,g-4)
    c: Coincident(g0,g-4)
FEATURE [PartDesign::Pad] Pad015
  BaseFeature = -> Pocket005
  Direction = (0,0,-1)
  Length = 3
  Length2 = 0
  Placement = pos=(0,0,0) rot=(-0.052562,0.997379,0.049714;1.78261rad)
  Profile = -> Sketch026
  ReferenceAxis = -> Sketch026 [N_Axis]
  Refine = true
  Reversed = true
  SideType = 0
  Suppressed = false
  Type = 0
  Type2 = 0
FEATURE [Sketcher::SketchObject] Sketch027  label="Sketch030"
  ArcFitTolerance = 1e-06
  AttachmentSupport = -> [XY_Plane029]
  ExternalTypes = [0]
  FullyConstrained = false
  MakeInternals = false
  MapMode = 5
  _ExternalGeoVersion = 0
  sketch-geometry (4):
    g0: LineSegment StartX=-27.5612 StartY=8.14378 StartZ=0 EndX=-27.5612 EndY=0 EndZ=0
    g1: LineSegment StartX=-27.5612 StartY=0 StartZ=0 EndX=13.0637 EndY=0 EndZ=0
    g2: LineSegment StartX=13.0637 StartY=0 StartZ=0 EndX=13.0637 EndY=8.14378 EndZ=0
    g3: LineSegment StartX=13.0637 StartY=8.14378 StartZ=0 EndX=-27.5612 EndY=8.14378 EndZ=0
  constraints (9):
    c: Coincident(g0,g1)
    c: Coincident(g1,g2)
    c: Coincident(g2,g3)
    c: Coincident(g3,g0)
    c: Vertical(g0)
    c: Vertical(g2)
    c: Horizontal(g1)
    c: Horizontal(g3)
    c: PointOnObject(g1,g-1)
FEATURE [PartDesign::Pocket] Pocket006
  BaseFeature = -> Pad015
  Direction = (0,0,-1)
  Length = 100
  Length2 = 100
  Placement = pos=(0,0,0) rot=(-0.052562,0.997379,0.049714;1.78261rad)
  Profile = -> Sketch027
  ReferenceAxis = -> Sketch027 [N_Axis]
  Refine = true
  Reversed = true
  SideType = 1
  Suppressed = false
  Type = 0
  Type2 = 0
FEATURE [PartDesign::Body] Body009
  AllowCompound = false
  Group = -> [DatumPlane008,Sketch022,Pad012,Sketch023,Pad013,Sketch024,Pad014,DatumPlane009,Sketch025,Pocket005,Sketch026,Pad015,Sketch027,Pocket006]
  Origin = -> Origin029
  Tip = -> Pocket006
FEATURE [App::Link] Link053  label="Mirror rails 004"
  LinkPlacement = pos=(169,30,-30) rot=(0,0,1;0rad)
  LinkedObject = -> Part013
  Placement = pos=(169,30,-30) rot=(0,0,1;0rad)
  expr: .Placement.Base.y = Spreadsheet.B5 - Spreadsheet.E2
FEATURE [Sketcher::SketchObject] Sketch028  label="Sketch031"
  ArcFitTolerance = 1e-06
  AttachmentSupport = -> [XY_Plane030]
  ExternalTypes = [0]
  FullyConstrained = true
  MakeInternals = false
  MapMode = 5
  _ExternalGeoVersion = 0
  expr: Constraints[10] = Spreadsheet.N15
  sketch-geometry (4):
    g0: LineSegment StartX=0 StartY=0 StartZ=0 EndX=0 EndY=-100 EndZ=0
    g1: LineSegment StartX=0 StartY=-100 StartZ=0 EndX=100 EndY=-100 EndZ=0
    g2: LineSegment StartX=100 StartY=-100 StartZ=0 EndX=100 EndY=0 EndZ=0
    g3: LineSegment StartX=100 StartY=0 StartZ=0 EndX=0 EndY=0 EndZ=0
  constraints (11):
    c: Coincident(g0,g1)
    c: Coincident(g1,g2)
    c: Coincident(g2,g3)
    c: Coincident(g3,g0)
    c: Vertical(g0)
    c: Vertical(g2)
    c: Horizontal(g1)
    c: Horizontal(g3)
    c: Coincident(g0,g-1)
    c: Equal(g0,g3)
    c: DistanceX(g3,g3) = 100
FEATURE [PartDesign::Pad] Pad016
  Direction = (0,0,1)
  Length = 6.35
  Length2 = 10
  Profile = -> Sketch028
  ReferenceAxis = -> Sketch028 [N_Axis]
  Refine = true
  Reversed = true
  SideType = 0
  Suppressed = false
  Type = 0
  Type2 = 0
  expr: Length = Spreadsheet.H1
FEATURE [PartDesign::Body] Body010
  AllowCompound = false
  Group = -> [Sketch028,Pad016]
  Origin = -> Origin030
  Placement = pos=(0,0,0) rot=(-0.05,1,0.049714;1.78261rad)
  Tip = -> Pad016
FEATURE [App::Part] Part013  label="Mirror rails 3"
  Group = -> [Body009,Body010]
  Origin = -> Origin028
FEATURE [PartDesign::Plane] DatumPlane010
  Length = 314.267
  MapMode = 1
  Placement = pos=(-5.44639,-5.45,-1.5) rot=(-0.230412,-0.551841,-0.801487;3.77945rad)
  ResizeMode = 0
  Width = 249.485
FEATURE [Sketcher::SketchObject] Sketch029  label="Sketch032"
  ArcFitTolerance = 1e-06
  AttachmentSupport = -> [DatumPlane010]
  ExternalTypes = [0]
  FullyConstrained = true
  MakeInternals = false
  MapMode = 5
  Placement = pos=(-5.44639,-5.45,-1.5) rot=(0.230412,0.551841,0.801487;2.50373rad)
  _ExternalGeoVersion = 0
  expr: Constraints[14] = Spreadsheet.B21
  expr: Constraints[15] = Spreadsheet.B24
  expr: Constraints[17] = Spreadsheet.B22 / 2
  sketch-geometry (6):
    g0: LineSegment StartX=40 StartY=80 StartZ=0 EndX=40 EndY=0 EndZ=0
    g1: LineSegment StartX=35 StartY=80 StartZ=0 EndX=35 EndY=5 EndZ=0
    g2: LineSegment StartX=35 StartY=80 StartZ=0 EndX=40 EndY=80 EndZ=0
    g3: LineSegment StartX=35 StartY=5 StartZ=0 EndX=-120 EndY=5 EndZ=0
    g4: LineSegment StartX=-120 StartY=5 StartZ=0 EndX=-120 EndY=0 EndZ=0
    g5: LineSegment StartX=-120 StartY=0 StartZ=0 EndX=40 EndY=0 EndZ=0
  constraints (18):
    c: Vertical(g0)
    c: Vertical(g1)
    c: Coincident(g2,g1)
    c: Coincident(g2,g0)
    c: Coincident(g3,g1)
    c: Horizontal(g3)
    c: Coincident(g4,g3)
    c: PointOnObject(g4,g-1)
    c: Vertical(g4)
    c: Coincident(g5,g0)
    c: Horizontal(g5)
    c: Horizontal(g2)
    c: Equal(g4,g2)
    c: DistanceX(g2,g2) = 5
    c: DistanceY(g0,g0) = 80
    c: DistanceX(g5,g5) = 160
    c: Coincident(g4,g5)
    c: Distance(g-2,g1) = 35
FEATURE [PartDesign::Pad] Pad017
  Direction = (0.661642,0.660415,0.355081)
  Length = 10
  Length2 = 5
  Placement = pos=(-5.44639,-5.45,-1.5) rot=(-0.230412,-0.551841,-0.801487;3.77945rad)
  Profile = -> Sketch029
  ReferenceAxis = -> Sketch029 [N_Axis]
  Refine = true
  SideType = 1
  Suppressed = false
  Type = 0
  Type2 = 0
  expr: Length = Spreadsheet.B23
FEATURE [Sketcher::SketchObject] Sketch030  label="Sketch033"
  ArcFitTolerance = 1e-06
  AttachmentSupport = -> [DatumPlane010]
  ExternalGeometry = -> [Pad017]
  ExternalTypes = [0]
  FullyConstrained = true
  MakeInternals = false
  MapMode = 5
  Placement = pos=(-5.44639,-5.45,-1.5) rot=(0.230412,0.551841,0.801487;2.50373rad)
  _ExternalGeoVersion = 0
  expr: Constraints[9] = Spreadsheet.B22
  sketch-geometry (74):
    g0: LineSegment [constr] StartX=-35 StartY=5 StartZ=0 EndX=-35 EndY=80 EndZ=0
    g1: LineSegment StartX=-35 StartY=80 StartZ=0 EndX=-120 EndY=80 EndZ=0
    g2: LineSegment StartX=-120 StartY=80 StartZ=0 EndX=-120 EndY=5 EndZ=0
    g3: LineSegment [constr] StartX=-35 StartY=80 StartZ=0 EndX=35 EndY=80 EndZ=0
    g4: LineSegment StartX=-35 StartY=80 StartZ=0 EndX=-35 EndY=15 EndZ=0
    g5: LineSegment StartX=-35 StartY=15 StartZ=0 EndX=25 EndY=15 EndZ=0
    g6: LineSegment StartX=35 StartY=80 StartZ=0 EndX=35 EndY=5 EndZ=0
    g7: LineSegment StartX=-120 StartY=5 StartZ=0 EndX=35 EndY=5 EndZ=0
    g8: LineSegment [constr] StartX=-113 StartY=73 StartZ=0 EndX=-113 EndY=15 EndZ=0
    g9: LineSegment [constr] StartX=-113 StartY=15 StartZ=0 EndX=-42 EndY=15 EndZ=0
    g10: LineSegment [constr] StartX=-42 StartY=15 StartZ=0 EndX=-42 EndY=73 EndZ=0
    g11: LineSegment [constr] StartX=-42 StartY=73 StartZ=0 EndX=-113 EndY=73 EndZ=0
    g12: LineSegment [constr] StartX=-113 StartY=73 StartZ=0 EndX=-113 EndY=80 EndZ=0
    g13: LineSegment [constr] StartX=-113 StartY=73 StartZ=0 EndX=-120 EndY=73 EndZ=0
    g14: LineSegment [constr] StartX=-42 StartY=15 StartZ=0 EndX=-35 EndY=15 EndZ=0
    g15: LineSegment [constr] StartX=-77.5 StartY=73 StartZ=0 EndX=-77.5 EndY=15 EndZ=0
    g16: LineSegment [constr] StartX=-113 StartY=44 StartZ=0 EndX=-42 EndY=44 EndZ=0
    g17: GeomPoint [constr] X=-77.5 Y=44 Z=0
    g18: LineSegment [constr] StartX=-86.6437 StartY=73 StartZ=0 EndX=-68.3563 EndY=15 EndZ=0
    g19: LineSegment [constr] StartX=-86.6437 StartY=15 StartZ=0 EndX=-68.3563 EndY=73 EndZ=0
    g20: LineSegment [constr] StartX=-42 StartY=55.1931 StartZ=0 EndX=-113 EndY=32.8069 EndZ=0
    g21: LineSegment [constr] StartX=-113 StartY=55.1931 StartZ=0 EndX=-42 EndY=32.8069 EndZ=0
    g22: Circle [constr] CenterX=-77.5 CenterY=44 CenterZ=0 NormalX=0 NormalY=0 NormalZ=1 AngleXU=0 Radius=9
    g23: Circle CenterX=-77.5 CenterY=44 CenterZ=0 NormalX=0 NormalY=0 NormalZ=1 AngleXU=0 Radius=6.5
    g24: ArcOfCircle CenterX=-77.5 CenterY=44 CenterZ=0 NormalX=0 NormalY=0 NormalZ=1 AngleXU=0 Radius=9 StartAngle=1.26536 EndAngle=1.87623
    g25: ArcOfCircle CenterX=-77.5 CenterY=44 CenterZ=0 NormalX=0 NormalY=0 NormalZ=1 AngleXU=0 Radius=9 StartAngle=5.97775 EndAngle=6.58862
    g26: ArcOfCircle CenterX=-77.5 CenterY=44 CenterZ=0 NormalX=0 NormalY=0 NormalZ=1 AngleXU=0 Radius=9 StartAngle=4.40696 EndAngle=5.01782
    g27: ArcOfCircle CenterX=-77.5 CenterY=44 CenterZ=0 NormalX=0 NormalY=0 NormalZ=1 AngleXU=0 Radius=9 StartAngle=2.83616 EndAngle=3.44703
    g28: LineSegment [constr] StartX=-80.2064 StartY=52.5835 StartZ=0 EndX=-74.7936 EndY=52.5835 EndZ=0
    g29: LineSegment [constr] StartX=-68.9165 StartY=46.7064 StartZ=0 EndX=-68.9165 EndY=41.2936 EndZ=0
    g30: LineSegment StartX=-74.7936 StartY=52.5835 StartZ=0 EndX=-68.3563 EndY=73 EndZ=0
    g31: LineSegment StartX=-80.2064 StartY=52.5835 StartZ=0 EndX=-86.6437 EndY=73 EndZ=0
    g32: LineSegment StartX=-86.6437 StartY=73 StartZ=0 EndX=-68.3563 EndY=73 EndZ=0
    g33: LineSegment StartX=-68.9165 StartY=46.7064 StartZ=0 EndX=-42 EndY=55.1931 EndZ=0
    g34: LineSegment StartX=-68.9165 StartY=41.2936 StartZ=0 EndX=-42 EndY=32.8069 EndZ=0
    g35: LineSegment StartX=-42 StartY=32.8069 StartZ=0 EndX=-42 EndY=55.1931 EndZ=0
    g36: LineSegment StartX=-80.2064 StartY=35.4165 StartZ=0 EndX=-86.6437 EndY=15 EndZ=0
    g37: LineSegment StartX=-86.6437 StartY=15 StartZ=0 EndX=-68.3563 EndY=15 EndZ=0
    g38: LineSegment StartX=-68.3563 StartY=15 StartZ=0 EndX=-74.7936 EndY=35.4165 EndZ=0
    g39: LineSegment StartX=-86.0835 StartY=46.7064 StartZ=0 EndX=-113 EndY=55.1931 EndZ=0
    g40: LineSegment StartX=-113 StartY=55.1931 StartZ=0 EndX=-113 EndY=32.8069 EndZ=0
    g41: LineSegment StartX=-113 StartY=32.8069 StartZ=0 EndX=-86.0835 EndY=41.2936 EndZ=0
    g42: LineSegment [constr] StartX=-92.5964 StartY=73 StartZ=0 EndX=-62.4036 EndY=15 EndZ=0
    g43: LineSegment [constr] StartX=-92.5964 StartY=15 StartZ=0 EndX=-62.4036 EndY=73 EndZ=0
    g44: LineSegment [constr] StartX=-113 StartY=62.4801 StartZ=0 EndX=-42 EndY=25.5199 EndZ=0
    g45: LineSegment [constr] StartX=-42 StartY=62.4801 StartZ=0 EndX=-113 EndY=25.5199 EndZ=0
    g46: ArcOfCircle CenterX=-77.5 CenterY=44 CenterZ=0 NormalX=0 NormalY=0 NormalZ=1 AngleXU=0 Radius=9 StartAngle=0.479966 EndAngle=1.09083
    g47: ArcOfCircle CenterX=-77.5 CenterY=44 CenterZ=0 NormalX=0 NormalY=0 NormalZ=1 AngleXU=0 Radius=9 StartAngle=5.19235 EndAngle=5.80322
    g48: ArcOfCircle CenterX=-77.5 CenterY=44 CenterZ=0 NormalX=0 NormalY=0 NormalZ=1 AngleXU=0 Radius=9 StartAngle=3.62156 EndAngle=4.23242
    g49: ArcOfCircle CenterX=-77.5 CenterY=44 CenterZ=0 NormalX=0 NormalY=0 NormalZ=1 AngleXU=0 Radius=9 StartAngle=2.05076 EndAngle=2.66163
    g50: LineSegment [constr] StartX=-73.3443 StartY=51.9831 StartZ=0 EndX=-69.5169 EndY=48.1557 EndZ=0
    g51: LineSegment [constr] StartX=-69.5169 StartY=39.8443 StartZ=0 EndX=-73.3443 EndY=36.0169 EndZ=0
    g52: LineSegment [constr] StartX=-69.5169 StartY=39.8443 StartZ=0 EndX=-68.9165 EndY=41.2936 EndZ=0
    g53: LineSegment [constr] StartX=-73.3443 StartY=36.0169 StartZ=0 EndX=-74.7936 EndY=35.4165 EndZ=0
    g54: LineSegment [constr] StartX=-74.7936 StartY=52.5835 StartZ=0 EndX=-73.3443 EndY=51.9831 EndZ=0
    g55: LineSegment [constr] StartX=-69.5169 StartY=48.1557 StartZ=0 EndX=-68.9165 EndY=46.7064 EndZ=0
    g56: LineSegment StartX=-85.4831 StartY=39.8443 StartZ=0 EndX=-113 EndY=25.5199 EndZ=0
    g57: LineSegment StartX=-81.6557 StartY=36.0169 StartZ=0 EndX=-92.5964 EndY=15 EndZ=0
    g58: LineSegment StartX=-92.5964 StartY=15 StartZ=0 EndX=-113 EndY=15 EndZ=0
    g59: LineSegment StartX=-113 StartY=15 StartZ=0 EndX=-113 EndY=25.5199 EndZ=0
    g60: LineSegment StartX=-73.3443 StartY=36.0169 StartZ=0 EndX=-62.4036 EndY=15 EndZ=0
    g61: LineSegment StartX=-62.4036 StartY=15 StartZ=0 EndX=-42 EndY=15 EndZ=0
    g62: LineSegment StartX=-42 StartY=15 StartZ=0 EndX=-42 EndY=25.5199 EndZ=0
    g63: LineSegment StartX=-42 StartY=25.5199 StartZ=0 EndX=-69.5169 EndY=39.8443 EndZ=0
    g64: LineSegment StartX=-73.3443 StartY=51.9831 StartZ=0 EndX=-62.4036 EndY=73 EndZ=0
    g65: LineSegment StartX=-62.4036 StartY=73 StartZ=0 EndX=-42 EndY=73 EndZ=0
    g66: LineSegment StartX=-42 StartY=73 StartZ=0 EndX=-42 EndY=62.4801 EndZ=0
    g67: LineSegment StartX=-42 StartY=62.4801 StartZ=0 EndX=-69.5169 EndY=48.1557 EndZ=0
    g68: LineSegment StartX=-81.6557 StartY=51.9831 StartZ=0 EndX=-92.5964 EndY=73 EndZ=0
    g69: LineSegment StartX=-92.5964 StartY=73 StartZ=0 EndX=-113 EndY=73 EndZ=0
    g70: LineSegment StartX=-113 StartY=73 StartZ=0 EndX=-113 EndY=62.4801 EndZ=0
    g71: LineSegment StartX=-113 StartY=62.4801 StartZ=0 EndX=-85.4831 EndY=48.1557 EndZ=0
    g72: LineSegment StartX=25 StartY=15 StartZ=0 EndX=25 EndY=80 EndZ=0
    g73: LineSegment StartX=25 StartY=80 StartZ=0 EndX=35 EndY=80 EndZ=0
  constraints (190):
    c: PointOnObject(g0,g-3)
    c: Vertical(g0)
    c: Coincident(g1,g0)
    c: Horizontal(g1)
    c: Coincident(g2,g1)
    c: Vertical(g2)
    c: Coincident(g3,g0)
    c: Coincident(g3,g-4)
    c: Horizontal(g3)
    c: DistanceX(g3,g3) = 70
    c: Coincident(g4,g0)
    c: PointOnObject(g4,g0)
    c: Coincident(g5,g4)
    c: Horizontal(g5)
    c: Coincident(g6,g-5)
    c: Coincident(g7,g2)
    c: Coincident(g7,g6)
    c: Coincident(g8,g9)
    c: Coincident(g9,g10)
    c: Coincident(g10,g11)
    c: Coincident(g11,g8)
    c: Vertical(g8)
    c: Vertical(g10)
    c: Horizontal(g11)
    c: Tangent(g9,g5)
    c: Coincident(g12,g8)
    c: PointOnObject(g12,g1)
    c: Vertical(g12)
    c: Coincident(g13,g8)
    c: PointOnObject(g13,g2)
    c: Horizontal(g13)
    c: Equal(g12,g13)
    c: Coincident(g2,g-3)
    c: Coincident(g14,g9)
    c: Coincident(g14,g4)
    c: Equal(g12,g14)
    c: Symmetric(g11,g11,g15)
    c: Symmetric(g9,g9,g15)
    c: Symmetric(g8,g8,g16)
    c: Symmetric(g10,g10,g16)
    c: Symmetric(g15,g15,g17)
    c: PointOnObject(g18,g11)
    c: PointOnObject(g18,g9)
    c: PointOnObject(g19,g9)
    c: PointOnObject(g19,g11)
    c: PointOnObject(g20,g10)
    c: PointOnObject(g20,g8)
    c: PointOnObject(g21,g8)
    c: PointOnObject(g17,g21)
    c: PointOnObject(g17,g19)
    c: PointOnObject(g17,g18)
    c: PointOnObject(g17,g20)
    c: PointOnObject(g21,g10)
    c: Diameter(g22) = 18
    c: Coincident(g22,g17)
    c: Diameter(g23) = 13
    c: Coincident(g23,g17)
    c: Coincident(g24,g17)
    c: PointOnObject(g24,g18)
    c: PointOnObject(g24,g19)
    c: Coincident(g25,g17)
    c: PointOnObject(g25,g20)
    c: PointOnObject(g25,g21)
    c: Coincident(g26,g17)
    c: PointOnObject(g26,g19)
    c: PointOnObject(g26,g18)
    c: Coincident(g27,g17)
    c: PointOnObject(g27,g21)
    c: PointOnObject(g27,g20)
    c: PointOnObject(g24,g22)
    c: PointOnObject(g25,g22)
    c: PointOnObject(g26,g22)
    c: PointOnObject(g27,g22)
    c: Coincident(g28,g24)
    c: Coincident(g28,g24)
    c: Horizontal(g28)
    c: Coincident(g29,g25)
    c: Coincident(g29,g25)
    c: Vertical(g29)
    c: Equal(g28,g29)
    c: Coincident(g30,g24)
    c: Coincident(g30,g19)
    c: Coincident(g31,g24)
    c: Coincident(g31,g18)
    c: Coincident(g32,g18)
    c: Coincident(g32,g30)
    c: Coincident(g33,g25)
    c: Coincident(g33,g20)
    c: Coincident(g34,g25)
    c: Coincident(g34,g21)
    c: Coincident(g35,g21)
    c: Coincident(g35,g20)
    c: Coincident(g36,g26)
    c: Coincident(g36,g19)
    c: Coincident(g37,g18)
    c: Coincident(g38,g18)
    c: Coincident(g39,g27)
    c: Coincident(g39,g21)
    c: Coincident(g40,g21)
    c: Coincident(g40,g20)
    c: Coincident(g41,g20)
    c: Coincident(g41,g27)
    c: PointOnObject(g42,g11)
    c: PointOnObject(g42,g9)
    c: PointOnObject(g43,g9)
    c: PointOnObject(g43,g11)
    c: PointOnObject(g17,g43)
    c: PointOnObject(g17,g42)
    c: PointOnObject(g17,g44)
    c: PointOnObject(g17,g45)
    c: Coincident(g46,g17)
    c: PointOnObject(g46,g43)
    c: PointOnObject(g46,g45)
    c: Coincident(g47,g17)
    c: PointOnObject(g47,g44)
    c: PointOnObject(g47,g42)
    c: Coincident(g48,g17)
    c: PointOnObject(g48,g43)
    c: PointOnObject(g48,g45)
    c: Coincident(g49,g17)
    c: PointOnObject(g49,g42)
    c: PointOnObject(g49,g44)
    c: Equal(g49,g22)
    c: Equal(g46,g22)
    c: Equal(g47,g22)
    c: Equal(g22,g48)
    c: Coincident(g50,g46)
    c: Coincident(g50,g46)
    c: Coincident(g51,g47)
    c: Coincident(g51,g47)
    c: Equal(g28,g50)
    c: Equal(g28,g51)
    c: Coincident(g38,g26)
    c: Angle(g30,g31) = 0.610865
    c: Coincident(g52,g47)
    c: Coincident(g52,g25)
    c: Coincident(g53,g47)
    c: Coincident(g53,g26)
    c: Equal(g53,g52)
    c: PointOnObject(g44,g10)
    c: PointOnObject(g44,g8)
    c: PointOnObject(g45,g8)
    c: PointOnObject(g45,g10)
    c: Coincident(g54,g24)
    c: Coincident(g54,g46)
    c: Coincident(g46,g55)
    c: Coincident(g55,g25)
    c: Equal(g54,g55)
    c: Coincident(g56,g48)
    c: Coincident(g56,g45)
    c: Coincident(g57,g48)
    c: Coincident(g57,g43)
    c: Coincident(g58,g43)
    c: Coincident(g58,g8)
    c: Coincident(g59,g8)
    c: Coincident(g59,g45)
    c: Coincident(g37,g19)
    c: Coincident(g60,g47)
    c: Coincident(g60,g42)
    c: Coincident(g61,g42)
    c: Coincident(g61,g9)
    c: Coincident(g62,g9)
    c: Coincident(g62,g44)
    c: Coincident(g63,g44)
    c: Coincident(g63,g47)
    c: Coincident(g64,g46)
    c: Coincident(g64,g43)
    c: Coincident(g65,g43)
    c: Coincident(g65,g10)
    c: Coincident(g66,g10)
    c: Coincident(g66,g45)
    c: Coincident(g67,g45)
    c: Coincident(g67,g46)
    c: Coincident(g68,g49)
    c: Coincident(g68,g42)
    c: Coincident(g69,g42)
    c: Coincident(g69,g8)
    c: Coincident(g70,g8)
    c: Coincident(g70,g44)
    c: Coincident(g71,g44)
    c: Coincident(g71,g49)
    c: DistanceX(g14,g14) = 7
    c: Coincident(g72,g5)
    c: PointOnObject(g72,g3)
    c: Vertical(g72)
    c: Coincident(g73,g72)
    c: Coincident(g73,g3)
    c: Distance(g7,g5) = 10
    c: Coincident(g6,g3)
    c: DistanceX(g73,g73) = 10
FEATURE [PartDesign::Pad] Pad018
  BaseFeature = -> Pad017
  Direction = (0.661642,0.660415,0.355081)
  Length = 5
  Length2 = 10
  Placement = pos=(-5.44639,-5.45,-1.5) rot=(-0.230412,-0.551841,-0.801487;3.77945rad)
  Profile = -> Sketch030
  ReferenceAxis = -> Sketch030 [N_Axis]
  Refine = true
  Reversed = true
  SideType = 0
  Suppressed = false
  Type = 0
  Type2 = 0
FEATURE [App::Link] Link054  label="Camera001"
  LinkPlacement = pos=(-170,-170,-170) rot=(0,0,1;0rad)
  LinkedObject = -> Part014
  Placement = pos=(-170,-170,-170) rot=(0,0,1;0rad)
FEATURE [App::Part] Part002  label="Frame"
  Group = -> [Link001,Link019,Link004,Link025,Link022,Link026,Link021,Link020,Link,Link032,Link033,Link034,Link035,Link011,Link012,Link013,Link014,Link015,Link016,Link036,Link037,Link038,Link039,Link040,Link041,Link050,Link051,Link052,Link053,Link054]
  Origin = -> Origin003
FEATURE [Sketcher::SketchObject] Sketch031  label="Sketch034"
  ArcFitTolerance = 1e-06
  AttachmentSupport = -> [XY_Plane032]
  ExternalTypes = [0]
  FullyConstrained = true
  MakeInternals = false
  MapMode = 5
  _ExternalGeoVersion = 0
  expr: Constraints[9] = Spreadsheet.E1
  sketch-geometry (13):
    g0: LineSegment StartX=0 StartY=60 StartZ=0 EndX=-30 EndY=60 EndZ=0
    g1: LineSegment StartX=-30 StartY=60 StartZ=0 EndX=-30 EndY=15.8579 EndZ=0
    g2: LineSegment StartX=15.8579 StartY=-30 StartZ=0 EndX=60 EndY=-30 EndZ=0
    g3: LineSegment StartX=60 StartY=-30 StartZ=0 EndX=60 EndY=0 EndZ=0
    g4: Circle CenterX=45 CenterY=-15 CenterZ=0 NormalX=0 NormalY=0 NormalZ=1 AngleXU=0 Radius=2.2
    g5: Circle CenterX=-15 CenterY=45 CenterZ=0 NormalX=0 NormalY=0 NormalZ=1 AngleXU=0 Radius=2.2
    g6: LineSegment [constr] StartX=-15 StartY=47.2 StartZ=0 EndX=-15 EndY=60 EndZ=0
    g7: LineSegment [constr] StartX=47.2 StartY=-15 StartZ=0 EndX=60 EndY=-15 EndZ=0
    g8: LineSegment [constr] StartX=-30 StartY=45 StartZ=0 EndX=-17.2 EndY=45 EndZ=0
    g9: ArcOfCircle CenterX=5 CenterY=5 CenterZ=0 NormalX=0 NormalY=0 NormalZ=1 AngleXU=0 Radius=5 StartAngle=3.14159 EndAngle=4.71239
    g10: LineSegment StartX=5 StartY=0 StartZ=0 EndX=60 EndY=0 EndZ=0
    g11: LineSegment StartX=0 StartY=5 StartZ=0 EndX=0 EndY=60 EndZ=0
    g12: LineSegment StartX=-30 StartY=15.8579 StartZ=0 EndX=15.8579 EndY=-30 EndZ=0
  constraints (39):
    c: PointOnObject(g0,g-2)
    c: Horizontal(g0)
    c: Vertical(g1)
    c: Horizontal(g2)
    c: Coincident(g3,g2)
    c: PointOnObject(g3,g-1)
    c: Vertical(g3)
    c: Coincident(g1,g0)
    c: Equal(g0,g3)
    c: DistanceX(g0,g0) = 30
    c: Diameter(g4) = 4.4
    c: Equal(g5,g4)
    c: PointOnObject(g6,g5)
    c: Symmetric(g0,g0,g6)
    c: Vertical(g6)
    c: PointOnObject(g7,g4)
    c: Horizontal(g7)
    c: Perpendicular(g4,g7)
    c: Perpendicular(g5,g6)
    c: Equal(g6,g7)
    c: Symmetric(g3,g2,g7)
    c: PointOnObject(g8,g1)
    c: PointOnObject(g8,g5)
    c: Horizontal(g8)
    c: Perpendicular(g5,g8)
    c: Equal(g6,g8)
    c: Coincident(g10,g3)
    c: Coincident(g11,g0)
    c: Vertical(g11)
    c: Horizontal(g10)
    c: Tangent(g10,g9) = -1.5708
    c: Tangent(g11,g9) = 1.5708
    c: Coincident(g12,g1)
    c: Coincident(g12,g2)
    c: Radius(g9) = 5
    c: Equal(g1,g2)
    c: Distance(g2,g-2) = 60
    c: Equal(g11,g10)
    c: Distance(g-1,g12) = 10
FEATURE [PartDesign::Pad] Pad019
  BaseFeature = -> Pad018
  Direction = (0,0,1)
  Length = 3
  Length2 = 10
  Placement = pos=(-5.44639,-5.45,-1.5) rot=(-0.230412,-0.551841,-0.801487;3.77945rad)
  Profile = -> Sketch031
  ReferenceAxis = -> Sketch031 [N_Axis]
  Refine = true
  SideType = 0
  Suppressed = false
  Type = 0
  Type2 = 0
FEATURE [Sketcher::SketchObject] Sketch032  label="Sketch035"
  ArcFitTolerance = 1e-06
  AttachmentSupport = -> [XY_Plane032]
  ExternalTypes = [0]
  FullyConstrained = false
  MakeInternals = false
  MapMode = 5
  _ExternalGeoVersion = 0
  sketch-geometry (4):
    g0: LineSegment StartX=-84.8731 StartY=80.5615 StartZ=0 EndX=-84.8731 EndY=-128.472 EndZ=0
    g1: LineSegment StartX=-84.8731 StartY=-128.472 StartZ=0 EndX=133.133 EndY=-128.472 EndZ=0
    g2: LineSegment StartX=133.133 StartY=-128.472 StartZ=0 EndX=133.133 EndY=80.5615 EndZ=0
    g3: LineSegment StartX=133.133 StartY=80.5615 StartZ=0 EndX=-84.8731 EndY=80.5615 EndZ=0
  constraints (8):
    c: Coincident(g0,g1)
    c: Coincident(g1,g2)
    c: Coincident(g2,g3)
    c: Coincident(g3,g0)
    c: Vertical(g0)
    c: Vertical(g2)
    c: Horizontal(g1)
    c: Horizontal(g3)
FEATURE [PartDesign::Pocket] Pocket007
  BaseFeature = -> Pad019
  Direction = (0,0,-1)
  Length = 100
  Length2 = 5
  Placement = pos=(-5.44639,-5.45,-1.5) rot=(-0.230412,-0.551841,-0.801487;3.77945rad)
  Profile = -> Sketch032
  ReferenceAxis = -> Sketch032 [N_Axis]
  Refine = true
  SideType = 0
  Suppressed = false
  Type = 0
  Type2 = 0
FEATURE [PartDesign::Fillet] Fillet010
  Base = -> Pocket007 [Edge171,Edge137,Edge138,Edge128,Edge132,Edge156,Edge112,Edge122,Edge146,Edge163,Edge154,Edge164,Edge153,Edge145,Edge148,Edge110,Edge107,Edge120,Edge117,Edge127,Edge150,Edge160,Edge114,Edge172,Edge158,Edge108,Edge118,Edge134,Edge142,Edge176,Edge178,Edge168,Edge140,Edge174,Edge166]
  BaseFeature = -> Pocket007
  Placement = pos=(-5.44639,-5.45,-1.5) rot=(-0.230412,-0.551841,-0.801487;3.77945rad)
  Radius = 1
  Refine = true
  SupportTransform = false
  Suppressed = false
  UseAllEdges = false
FEATURE [PartDesign::Fillet] Fillet011
  Base = -> Fillet010 [Edge102,Edge131,Edge108,Edge106,Edge272,Edge119,Edge271,Edge274,Edge120,Edge277,Edge280,Edge123,Edge281,Edge124,Edge111,Edge269,Edge112]
  BaseFeature = -> Fillet010
  Placement = pos=(-5.44639,-5.45,-1.5) rot=(-0.230412,-0.551841,-0.801487;3.77945rad)
  Radius = 1
  Refine = true
  SupportTransform = false
  Suppressed = false
  UseAllEdges = false
FEATURE [PartDesign::Fillet] Fillet012
  Base = -> Fillet011 [Edge277,Edge278,Edge288,Edge91,Edge88]
  BaseFeature = -> Fillet011
  Placement = pos=(-5.44639,-5.45,-1.5) rot=(-0.230412,-0.551841,-0.801487;3.77945rad)
  Radius = 3
  Refine = true
  SupportTransform = false
  Suppressed = false
  UseAllEdges = false
FEATURE [PartDesign::Body] Body011
  AllowCompound = false
  Group = -> [DatumPlane010,Sketch029,Pad017,Sketch030,Pad018,Sketch031,Pad019,Sketch032,Pocket007,Fillet010,Fillet011,Fillet012]
  Origin = -> Origin032
  Tip = -> Fillet012
FEATURE [App::Part] Part014  label="Camera"
  Group = -> [Body011]
  Origin = -> Origin031
FEATURE [App::Point] Origin033  label="Origin"
  Role = Origin
FEATURE [App::Point] Origin034  label="Origin"
  Role = Origin
FEATURE [App::Point] Origin035  label="Origin"
  Role = Origin
FEATURE [App::Point] Origin036  label="Origin"
  Role = Origin
FEATURE [App::Point] Origin037  label="Origin"
  Role = Origin
FEATURE [App::Point] Origin038  label="Origin"
  Role = Origin
FEATURE [App::Point] Origin039  label="Origin"
  Role = Origin
FEATURE [App::Point] Origin040  label="Origin"
  Role = Origin
FEATURE [App::Point] Origin041  label="Origin"
  Role = Origin
FEATURE [App::Point] Origin042  label="Origin"
  Role = Origin
FEATURE [App::Point] Origin043  label="Origin"
  Role = Origin
FEATURE [App::Point] Origin044  label="Origin"
  Role = Origin
FEATURE [App::Point] Origin045  label="Origin"
  Role = Origin
FEATURE [App::Point] Origin046  label="Origin"
  Role = Origin
FEATURE [App::Point] Origin047  label="Origin"
  Role = Origin
FEATURE [App::Point] Origin048  label="Origin"
  Role = Origin
FEATURE [App::Point] Origin049  label="Origin"
  Role = Origin
FEATURE [App::Point] Origin050  label="Origin"
  Role = Origin
FEATURE [App::Point] Origin051  label="Origin"
  Role = Origin
FEATURE [App::Point] Origin052  label="Origin"
  Role = Origin
FEATURE [App::Point] Origin053  label="Origin"
  Role = Origin
FEATURE [App::Point] Origin054  label="Origin"
  Role = Origin
FEATURE [App::Point] Origin055  label="Origin"
  Role = Origin
FEATURE [App::Point] Origin056  label="Origin"
  Role = Origin
FEATURE [App::Point] Origin057  label="Origin"
  Role = Origin
FEATURE [App::Point] Origin058  label="Origin"
  Role = Origin
FEATURE [App::Point] Origin059  label="Origin"
  Role = Origin
FEATURE [App::Point] Origin060  label="Origin"
  Role = Origin
FEATURE [App::Point] Origin061  label="Origin"
  Role = Origin
FEATURE [App::Point] Origin062  label="Origin"
  Role = Origin
FEATURE [App::Point] Origin063  label="Origin"
  Role = Origin
FEATURE [App::Point] Origin064  label="Origin"
  Role = Origin
FEATURE [Measure::MeasureArea] Area  label="Area: 28.88 cm^2"
  Area = 2887.53
  Elements = -> [Part002]
FEATURE [App::DocumentObjectGroup] Measurements
  Group = -> [Area]
